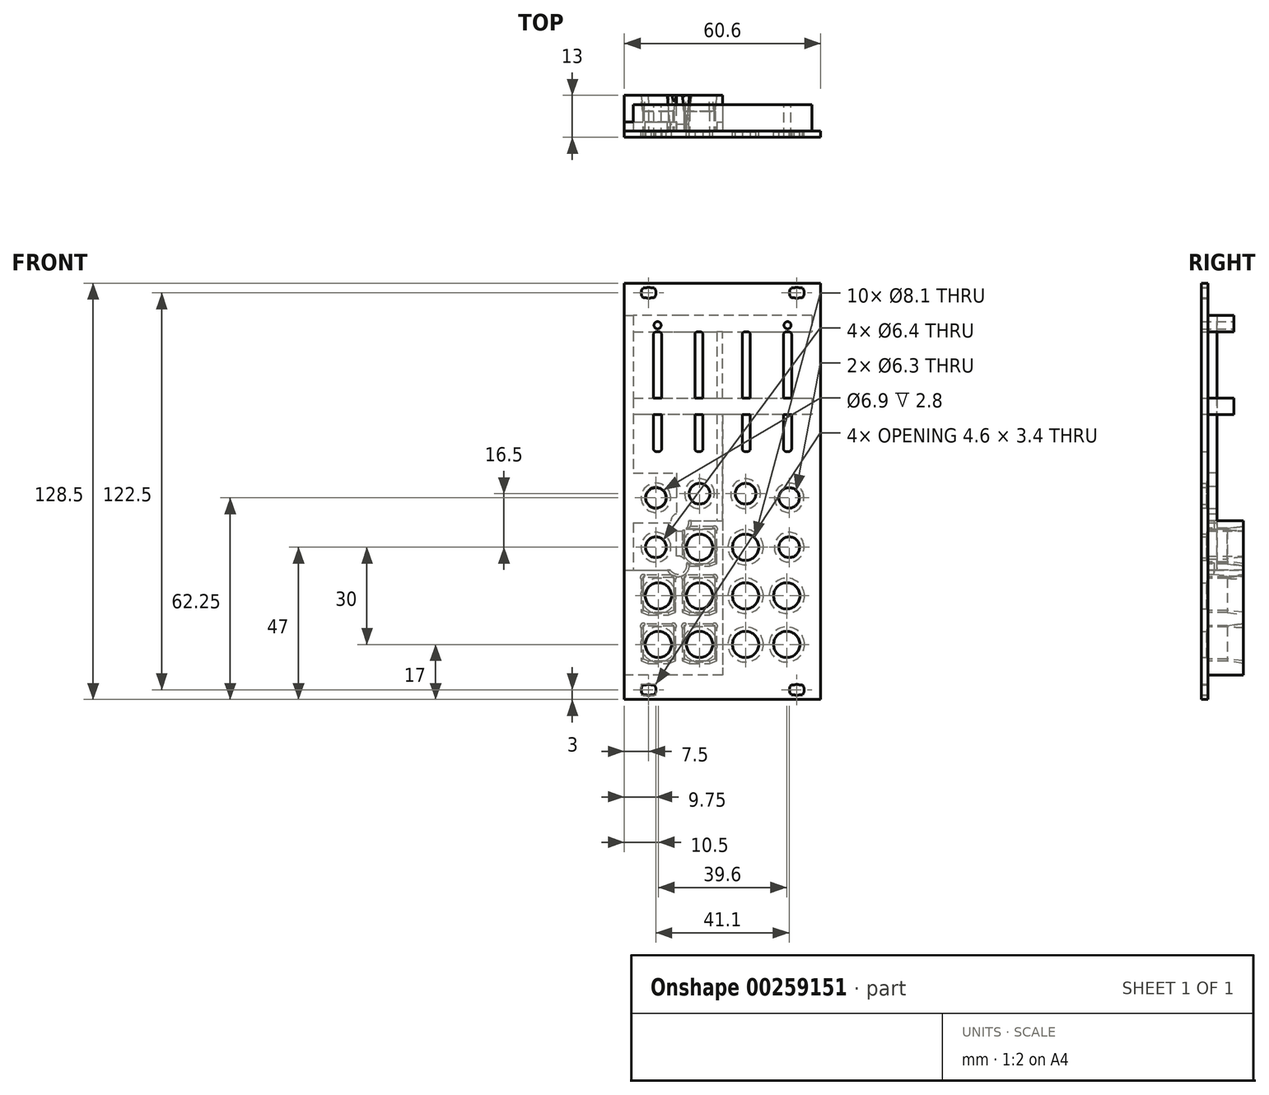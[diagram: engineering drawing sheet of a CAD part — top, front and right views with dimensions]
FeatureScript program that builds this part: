
annotation { "Feature Type Name" : "Feature", "Feature Type Description" : "" }
export const myFeature = defineFeature(function(context is Context, id is Id, definition is map)
    precondition{}
    {
        {
            var Q0;
            Q0=qCreatedBy(makeId("Front.planeOp"),FACE);
            var sketch = newSketch(context, id + "F0", { "sketchPlane" : qUnion([Q0])});
            skLineSegment(sketch, "E0", {"start": v(23.72, -59.75) * mm, "end": v(24.62, -59.75) * mm});
            skLineSegment(sketch, "E1", {"start": v(21.22, -59.75) * mm, "end": v(22.12, -59.75) * mm});
            skLineSegment(sketch, "E2", {"start": v(23.72, -62.75) * mm, "end": v(24.62, -62.75) * mm});
            skLineSegment(sketch, "E3", {"start": v(21.22, -62.75) * mm, "end": v(22.12, -62.75) * mm});
            skLineSegment(sketch, "E4", {"start": v(21.22, 59.75) * mm, "end": v(22.12, 59.75) * mm});
            skLineSegment(sketch, "E5", {"start": v(23.72, 59.75) * mm, "end": v(24.62, 59.75) * mm});
            skLineSegment(sketch, "E6", {"start": v(21.22, 62.75) * mm, "end": v(22.12, 62.75) * mm});
            skLineSegment(sketch, "E7", {"start": v(23.72, 62.75) * mm, "end": v(24.62, 62.75) * mm});
            skLineSegment(sketch, "E8", {"start": v(-30.3, -64.25) * mm, "end": v(-30.3, -61.25) * mm});
            skLineSegment(sketch, "E9", {"start": v(-30.3, 64.25) * mm, "end": v(30.3, 64.25) * mm});
            skLineSegment(sketch, "E10", {"start": v(30.3, -64.25) * mm, "end": v(30.3, 64.25) * mm});
            skLineSegment(sketch, "E11", {"start": v(-30.3, -64.25) * mm, "end": v(30.3, -64.25) * mm});
            skLineSegment(sketch, "E12", {"start": v(-30.3, -64.25) * mm, "end": v(-30.3, 64.25) * mm});
            skLineSegment(sketch, "E13", {"start": v(-22, -59.75) * mm, "end": v(-21.1, -59.75) * mm});
            skLineSegment(sketch, "E14", {"start": v(-24.5, -59.75) * mm, "end": v(-23.6, -59.75) * mm});
            skLineSegment(sketch, "E15", {"start": v(-22, -62.75) * mm, "end": v(-21.1, -62.75) * mm});
            skLineSegment(sketch, "E16", {"start": v(-24.5, -62.75) * mm, "end": v(-23.6, -62.75) * mm});
            skLineSegment(sketch, "E17", {"start": v(-22, 62.75) * mm, "end": v(-21.1, 62.75) * mm});
            skLineSegment(sketch, "E18", {"start": v(-24.5, 62.75) * mm, "end": v(-23.6, 62.75) * mm});
            skLineSegment(sketch, "E19", {"start": v(-22, 59.75) * mm, "end": v(-21.1, 59.75) * mm});
            skLineSegment(sketch, "E20", {"start": v(-24.5, 59.75) * mm, "end": v(-23.6, 59.75) * mm});
            skArc(sketch, "E21", {"start": v(21.22, -59.75) * mm, "mid": v(20.62, -61.25) * mm, "end": v(21.22, -62.75) * mm});
            skArc(sketch, "E22", {"start": v(24.62, -62.75) * mm, "mid": v(25.22, -61.25) * mm, "end": v(24.62, -59.75) * mm});
            skArc(sketch, "E23", {"start": v(23.72, -59.75) * mm, "mid": v(22.92, -59.55) * mm, "end": v(22.12, -59.75) * mm});
            skArc(sketch, "E24", {"start": v(22.12, -62.75) * mm, "mid": v(22.92, -62.95) * mm, "end": v(23.72, -62.75) * mm});
            skArc(sketch, "E25", {"start": v(22.12, 59.75) * mm, "mid": v(22.92, 59.55) * mm, "end": v(23.72, 59.75) * mm});
            skArc(sketch, "E26", {"start": v(23.72, 62.75) * mm, "mid": v(22.92, 62.95) * mm, "end": v(22.12, 62.75) * mm});
            skArc(sketch, "E27", {"start": v(24.62, 59.75) * mm, "mid": v(25.22, 61.25) * mm, "end": v(24.62, 62.75) * mm});
            skArc(sketch, "E28", {"start": v(21.22, 62.75) * mm, "mid": v(20.62, 61.25) * mm, "end": v(21.22, 59.75) * mm});
            skArc(sketch, "E29", {"start": v(-24.5, -59.75) * mm, "mid": v(-25.1, -61.25) * mm, "end": v(-24.5, -62.75) * mm});
            skArc(sketch, "E30", {"start": v(-21.1, -62.75) * mm, "mid": v(-20.5, -61.25) * mm, "end": v(-21.1, -59.75) * mm});
            skArc(sketch, "E31", {"start": v(-22, -59.75) * mm, "mid": v(-22.8, -59.55) * mm, "end": v(-23.6, -59.75) * mm});
            skArc(sketch, "E32", {"start": v(-23.6, -62.75) * mm, "mid": v(-22.8, -62.95) * mm, "end": v(-22, -62.75) * mm});
            skArc(sketch, "E33", {"start": v(-24.5, 62.75) * mm, "mid": v(-25.1, 61.25) * mm, "end": v(-24.5, 59.75) * mm});
            skArc(sketch, "E34", {"start": v(-21.1, 59.75) * mm, "mid": v(-20.5, 61.25) * mm, "end": v(-21.1, 62.75) * mm});
            skArc(sketch, "E35", {"start": v(-22, 62.75) * mm, "mid": v(-22.8, 62.95) * mm, "end": v(-23.6, 62.75) * mm});
            skArc(sketch, "E36", {"start": v(-23.6, 59.75) * mm, "mid": v(-22.8, 59.55) * mm, "end": v(-22, 59.75) * mm});
            skLineSegment(sketch, "E37", {"start": v(13.3, -22.75) * mm, "end": v(14.3, -22.75) * mm});
            skLineSegment(sketch, "E38", {"start": v(13.8, -23.25) * mm, "end": v(13.8, -22.25) * mm});
            skLineSegment(sketch, "E39", {"start": v(-20.55, -2.5) * mm, "end": v(-20.55, -1.5) * mm});
            skLineSegment(sketch, "E40", {"start": v(-21.05, -2) * mm, "end": v(-20.05, -2) * mm});
            skCircle(sketch, "E41", {"center": v(-20.55, -2) * mm, "radius": 3.15 * mm});
            skLineSegment(sketch, "E42", {"start": v(20.55, -2.5) * mm, "end": v(20.55, -1.5) * mm});
            skLineSegment(sketch, "E43", {"start": v(20.05, -2) * mm, "end": v(21.05, -2) * mm});
            skCircle(sketch, "E44", {"center": v(20.55, -2) * mm, "radius": 3.15 * mm});
            skLineSegment(sketch, "E45", {"start": v(6.05, 30.75) * mm, "end": v(6.05, 48.35) * mm});
            skLineSegment(sketch, "E46", {"start": v(6.05, 13.15) * mm, "end": v(6.05, 30.75) * mm});
            skLineSegment(sketch, "E47", {"start": v(6.95, 12.25) * mm, "end": v(7.65, 12.25) * mm});
            skLineSegment(sketch, "E48", {"start": v(7.3, 30.25) * mm, "end": v(7.3, 31.25) * mm});
            skLineSegment(sketch, "E49", {"start": v(8.55, 13.15) * mm, "end": v(8.55, 30.75) * mm});
            skLineSegment(sketch, "E50", {"start": v(6.8, 30.75) * mm, "end": v(7.8, 30.75) * mm});
            skLineSegment(sketch, "E51", {"start": v(6.95, 49.25) * mm, "end": v(7.65, 49.25) * mm});
            skLineSegment(sketch, "E52", {"start": v(8.55, 30.75) * mm, "end": v(8.55, 48.35) * mm});
            skArc(sketch, "E53", {"start": v(6.05, 13.15) * mm, "mid": v(6.31, 12.51) * mm, "end": v(6.95, 12.25) * mm});
            skArc(sketch, "E54", {"start": v(6.95, 49.25) * mm, "mid": v(6.31, 48.99) * mm, "end": v(6.05, 48.35) * mm});
            skArc(sketch, "E55", {"start": v(7.65, 12.25) * mm, "mid": v(8.29, 12.51) * mm, "end": v(8.55, 13.15) * mm});
            skArc(sketch, "E56", {"start": v(8.55, 48.35) * mm, "mid": v(8.29, 48.99) * mm, "end": v(7.65, 49.25) * mm});
            skLineSegment(sketch, "E57", {"start": v(-8.55, 30.75) * mm, "end": v(-8.55, 48.35) * mm});
            skLineSegment(sketch, "E58", {"start": v(-8.55, 13.15) * mm, "end": v(-8.55, 30.75) * mm});
            skLineSegment(sketch, "E59", {"start": v(-7.65, 12.25) * mm, "end": v(-6.95, 12.25) * mm});
            skLineSegment(sketch, "E60", {"start": v(-7.3, 30.25) * mm, "end": v(-7.3, 31.25) * mm});
            skLineSegment(sketch, "E61", {"start": v(-6.05, 13.15) * mm, "end": v(-6.05, 30.75) * mm});
            skLineSegment(sketch, "E62", {"start": v(-7.8, 30.75) * mm, "end": v(-6.8, 30.75) * mm});
            skLineSegment(sketch, "E63", {"start": v(-7.65, 49.25) * mm, "end": v(-6.95, 49.25) * mm});
            skLineSegment(sketch, "E64", {"start": v(-6.05, 30.75) * mm, "end": v(-6.05, 48.35) * mm});
            skArc(sketch, "E65", {"start": v(-8.55, 13.15) * mm, "mid": v(-8.29, 12.51) * mm, "end": v(-7.65, 12.25) * mm});
            skArc(sketch, "E66", {"start": v(-7.65, 49.25) * mm, "mid": v(-8.29, 48.99) * mm, "end": v(-8.55, 48.35) * mm});
            skArc(sketch, "E67", {"start": v(-6.95, 12.25) * mm, "mid": v(-6.31, 12.51) * mm, "end": v(-6.05, 13.15) * mm});
            skArc(sketch, "E68", {"start": v(-6.05, 48.35) * mm, "mid": v(-6.31, 48.99) * mm, "end": v(-6.95, 49.25) * mm});
            skLineSegment(sketch, "E69", {"start": v(18.8, 30.75) * mm, "end": v(18.8, 48.35) * mm});
            skLineSegment(sketch, "E70", {"start": v(18.8, 13.15) * mm, "end": v(18.8, 30.75) * mm});
            skLineSegment(sketch, "E71", {"start": v(19.7, 12.25) * mm, "end": v(20.4, 12.25) * mm});
            skLineSegment(sketch, "E72", {"start": v(20.05, 30.25) * mm, "end": v(20.05, 31.25) * mm});
            skLineSegment(sketch, "E73", {"start": v(21.3, 13.15) * mm, "end": v(21.3, 30.75) * mm});
            skLineSegment(sketch, "E74", {"start": v(19.55, 30.75) * mm, "end": v(20.55, 30.75) * mm});
            skLineSegment(sketch, "E75", {"start": v(19.7, 49.25) * mm, "end": v(20.4, 49.25) * mm});
            skLineSegment(sketch, "E76", {"start": v(21.3, 30.75) * mm, "end": v(21.3, 48.35) * mm});
            skArc(sketch, "E77", {"start": v(18.8, 13.15) * mm, "mid": v(19.06, 12.51) * mm, "end": v(19.7, 12.25) * mm});
            skArc(sketch, "E78", {"start": v(19.7, 49.25) * mm, "mid": v(19.06, 48.99) * mm, "end": v(18.8, 48.35) * mm});
            skArc(sketch, "E79", {"start": v(20.4, 12.25) * mm, "mid": v(21.04, 12.51) * mm, "end": v(21.3, 13.15) * mm});
            skArc(sketch, "E80", {"start": v(21.3, 48.35) * mm, "mid": v(21.04, 48.99) * mm, "end": v(20.4, 49.25) * mm});
            skLineSegment(sketch, "E81", {"start": v(-21.3, 30.75) * mm, "end": v(-21.3, 48.35) * mm});
            skLineSegment(sketch, "E82", {"start": v(-21.3, 13.15) * mm, "end": v(-21.3, 30.75) * mm});
            skLineSegment(sketch, "E83", {"start": v(-20.4, 12.25) * mm, "end": v(-19.7, 12.25) * mm});
            skLineSegment(sketch, "E84", {"start": v(-20.05, 30.25) * mm, "end": v(-20.05, 31.25) * mm});
            skLineSegment(sketch, "E85", {"start": v(-18.8, 13.15) * mm, "end": v(-18.8, 30.75) * mm});
            skLineSegment(sketch, "E86", {"start": v(-20.55, 30.75) * mm, "end": v(-19.55, 30.75) * mm});
            skLineSegment(sketch, "E87", {"start": v(-20.4, 49.25) * mm, "end": v(-19.7, 49.25) * mm});
            skLineSegment(sketch, "E88", {"start": v(-18.8, 30.75) * mm, "end": v(-18.8, 48.35) * mm});
            skArc(sketch, "E89", {"start": v(-21.3, 13.15) * mm, "mid": v(-21.04, 12.51) * mm, "end": v(-20.4, 12.25) * mm});
            skArc(sketch, "E90", {"start": v(-20.4, 49.25) * mm, "mid": v(-21.04, 48.99) * mm, "end": v(-21.3, 48.35) * mm});
            skArc(sketch, "E91", {"start": v(-19.7, 12.25) * mm, "mid": v(-19.06, 12.51) * mm, "end": v(-18.8, 13.15) * mm});
            skArc(sketch, "E92", {"start": v(-18.8, 48.35) * mm, "mid": v(-19.06, 48.99) * mm, "end": v(-19.7, 49.25) * mm});
            skCircle(sketch, "E93", {"center": v(-20.05, 51.25) * mm, "radius": 1.1 * mm});
            skLineSegment(sketch, "E94", {"start": v(-14.3, -22.75) * mm, "end": v(-13.3, -22.75) * mm});
            skLineSegment(sketch, "E95", {"start": v(-13.8, -23.25) * mm, "end": v(-13.8, -22.25) * mm});
            skLineSegment(sketch, "E96", {"start": v(13.2, -10) * mm, "end": v(13.2, -9) * mm});
            skLineSegment(sketch, "E97", {"start": v(12.7, -9.5) * mm, "end": v(13.7, -9.5) * mm});
            skLineSegment(sketch, "E98", {"start": v(-13.2, -10) * mm, "end": v(-13.2, -9) * mm});
            skLineSegment(sketch, "E99", {"start": v(-13.7, -9.5) * mm, "end": v(-12.7, -9.5) * mm});
            skLineSegment(sketch, "E100", {"start": v(7.1, -1.25) * mm, "end": v(7.1, -0.25) * mm});
            skLineSegment(sketch, "E101", {"start": v(6.6, -0.75) * mm, "end": v(7.6, -0.75) * mm});
            skCircle(sketch, "E102", {"center": v(7.1, -0.75) * mm, "radius": 3.2 * mm});
            skLineSegment(sketch, "E103", {"start": v(-7.1, -1.25) * mm, "end": v(-7.1, -0.25) * mm});
            skLineSegment(sketch, "E104", {"start": v(-7.6, -0.75) * mm, "end": v(-6.6, -0.75) * mm});
            skCircle(sketch, "E105", {"center": v(-7.1, -0.75) * mm, "radius": 3.2 * mm});
            skLineSegment(sketch, "E106", {"start": v(20.55, -17.75) * mm, "end": v(20.55, -16.75) * mm});
            skLineSegment(sketch, "E107", {"start": v(20.05, -17.25) * mm, "end": v(21.05, -17.25) * mm});
            skCircle(sketch, "E108", {"center": v(20.55, -17.25) * mm, "radius": 3.2 * mm});
            skLineSegment(sketch, "E109", {"start": v(-20.55, -17.75) * mm, "end": v(-20.55, -16.75) * mm});
            skLineSegment(sketch, "E110", {"start": v(-21.05, -17.25) * mm, "end": v(-20.05, -17.25) * mm});
            skCircle(sketch, "E111", {"center": v(-20.55, -17.25) * mm, "radius": 3.2 * mm});
            skLineSegment(sketch, "E112", {"start": v(6.35, -17.25) * mm, "end": v(7.85, -17.25) * mm});
            skLineSegment(sketch, "E113", {"start": v(7.1, -18) * mm, "end": v(7.1, -16.5) * mm});
            skCircle(sketch, "E114", {"center": v(7.1, -17.25) * mm, "radius": 4.05 * mm});
            skLineSegment(sketch, "E115", {"start": v(19.05, -32.25) * mm, "end": v(20.55, -32.25) * mm});
            skLineSegment(sketch, "E116", {"start": v(19.8, -33) * mm, "end": v(19.8, -31.5) * mm});
            skCircle(sketch, "E117", {"center": v(19.8, -32.25) * mm, "radius": 4.05 * mm});
            skLineSegment(sketch, "E118", {"start": v(6.35, -32.25) * mm, "end": v(7.85, -32.25) * mm});
            skLineSegment(sketch, "E119", {"start": v(7.1, -33) * mm, "end": v(7.1, -31.5) * mm});
            skCircle(sketch, "E120", {"center": v(7.1, -32.25) * mm, "radius": 4.05 * mm});
            skLineSegment(sketch, "E121", {"start": v(19.05, -47.25) * mm, "end": v(20.55, -47.25) * mm});
            skLineSegment(sketch, "E122", {"start": v(19.8, -48) * mm, "end": v(19.8, -46.5) * mm});
            skCircle(sketch, "E123", {"center": v(19.8, -47.25) * mm, "radius": 4.05 * mm});
            skLineSegment(sketch, "E124", {"start": v(6.35, -47.25) * mm, "end": v(7.85, -47.25) * mm});
            skLineSegment(sketch, "E125", {"start": v(7.1, -48) * mm, "end": v(7.1, -46.5) * mm});
            skCircle(sketch, "E126", {"center": v(7.1, -47.25) * mm, "radius": 4.05 * mm});
            skLineSegment(sketch, "E127", {"start": v(-7.85, -17.25) * mm, "end": v(-6.35, -17.25) * mm});
            skLineSegment(sketch, "E128", {"start": v(-7.1, -18) * mm, "end": v(-7.1, -16.5) * mm});
            skCircle(sketch, "E129", {"center": v(-7.1, -17.25) * mm, "radius": 4.05 * mm});
            skLineSegment(sketch, "E130", {"start": v(-20.55, -32.25) * mm, "end": v(-19.05, -32.25) * mm});
            skLineSegment(sketch, "E131", {"start": v(-19.8, -33) * mm, "end": v(-19.8, -31.5) * mm});
            skCircle(sketch, "E132", {"center": v(-19.8, -32.25) * mm, "radius": 4.05 * mm});
            skLineSegment(sketch, "E133", {"start": v(-7.85, -32.25) * mm, "end": v(-6.35, -32.25) * mm});
            skLineSegment(sketch, "E134", {"start": v(-7.1, -33) * mm, "end": v(-7.1, -31.5) * mm});
            skCircle(sketch, "E135", {"center": v(-7.1, -32.25) * mm, "radius": 4.05 * mm});
            skLineSegment(sketch, "E136", {"start": v(-20.55, -47.25) * mm, "end": v(-19.05, -47.25) * mm});
            skLineSegment(sketch, "E137", {"start": v(-19.8, -48) * mm, "end": v(-19.8, -46.5) * mm});
            skCircle(sketch, "E138", {"center": v(-19.8, -47.25) * mm, "radius": 4.05 * mm});
            skLineSegment(sketch, "E139", {"start": v(-7.85, -47.25) * mm, "end": v(-6.35, -47.25) * mm});
            skLineSegment(sketch, "E140", {"start": v(-7.1, -48) * mm, "end": v(-7.1, -46.5) * mm});
            skCircle(sketch, "E141", {"center": v(-7.1, -47.25) * mm, "radius": 4.05 * mm});
            skLineSegment(sketch, "E142", {"start": v(19.42, 51.25) * mm, "end": v(20.69, 51.25) * mm});
            skLineSegment(sketch, "E143", {"start": v(20.05, 50.62) * mm, "end": v(20.05, 51.89) * mm});
            skCircle(sketch, "E144", {"center": v(20.05, 51.25) * mm, "radius": 1.1 * mm});
            skLineSegment(sketch, "E145", {"start": v(-20.69, 51.25) * mm, "end": v(-19.41, 51.25) * mm});
            skLineSegment(sketch, "E146", {"start": v(-20.05, 50.62) * mm, "end": v(-20.05, 51.89) * mm});
            skCircle(sketch, "E147", {"center": v(-13.8, -22.75) * mm, "radius": 0.75 * mm, "construction": true});
            skCircle(sketch, "E148", {"center": v(-13.2, -9.5) * mm, "radius": 1 * mm, "construction": true});
            skCircle(sketch, "E149", {"center": v(13.2, -9.5) * mm, "radius": 1 * mm, "construction": true});
            skCircle(sketch, "E150", {"center": v(13.8, -22.75) * mm, "radius": 0.75 * mm, "construction": true});
            skSolve(sketch);
        }
        {
            var Q0;
            Q0=qSketchRegion(id+"F0",true);
            extrude(context, id + "F1", {"entities" : qUnion([Q0]), "depth" : 2 * mm});
        }
        {
            var Q0;
            Q0=makeQuery(id+"F1.opExtrude","CAP_FACE",FACE,{"disambiguationData":[OSD([sQuery(id+"F0.wireOp",EDGE,"E0"),sQuery(id+"F0.wireOp",EDGE,"E1"),sQuery(id+"F0.wireOp",EDGE,"E2"),sQuery(id+"F0.wireOp",EDGE,"E3"),sQuery(id+"F0.wireOp",EDGE,"E4"),sQuery(id+"F0.wireOp",EDGE,"E5"),sQuery(id+"F0.wireOp",EDGE,"E6"),sQuery(id+"F0.wireOp",EDGE,"E7"),sQuery(id+"F0.wireOp",EDGE,"E9"),sQuery(id+"F0.wireOp",EDGE,"E10"),sQuery(id+"F0.wireOp",EDGE,"E11"),sQuery(id+"F0.wireOp",EDGE,"E12"),sQuery(id+"F0.wireOp",EDGE,"E13"),sQuery(id+"F0.wireOp",EDGE,"E14"),sQuery(id+"F0.wireOp",EDGE,"E15"),sQuery(id+"F0.wireOp",EDGE,"E16"),sQuery(id+"F0.wireOp",EDGE,"E17"),sQuery(id+"F0.wireOp",EDGE,"E18"),sQuery(id+"F0.wireOp",EDGE,"E19"),sQuery(id+"F0.wireOp",EDGE,"E20"),sQuery(id+"F0.wireOp",EDGE,"E21"),sQuery(id+"F0.wireOp",EDGE,"E22"),sQuery(id+"F0.wireOp",EDGE,"E23"),sQuery(id+"F0.wireOp",EDGE,"E24"),sQuery(id+"F0.wireOp",EDGE,"E25"),sQuery(id+"F0.wireOp",EDGE,"E26"),sQuery(id+"F0.wireOp",EDGE,"E27"),sQuery(id+"F0.wireOp",EDGE,"E28"),sQuery(id+"F0.wireOp",EDGE,"E29"),sQuery(id+"F0.wireOp",EDGE,"E30"),sQuery(id+"F0.wireOp",EDGE,"E31"),sQuery(id+"F0.wireOp",EDGE,"E32"),sQuery(id+"F0.wireOp",EDGE,"E33"),sQuery(id+"F0.wireOp",EDGE,"E34"),sQuery(id+"F0.wireOp",EDGE,"E35"),sQuery(id+"F0.wireOp",EDGE,"E36"),sQuery(id+"F0.wireOp",EDGE,"E41"),sQuery(id+"F0.wireOp",EDGE,"E44"),sQuery(id+"F0.wireOp",EDGE,"E45"),sQuery(id+"F0.wireOp",EDGE,"E46"),sQuery(id+"F0.wireOp",EDGE,"E47"),sQuery(id+"F0.wireOp",EDGE,"E49"),sQuery(id+"F0.wireOp",EDGE,"E51"),sQuery(id+"F0.wireOp",EDGE,"E52"),sQuery(id+"F0.wireOp",EDGE,"E53"),sQuery(id+"F0.wireOp",EDGE,"E54"),sQuery(id+"F0.wireOp",EDGE,"E55"),sQuery(id+"F0.wireOp",EDGE,"E56"),sQuery(id+"F0.wireOp",EDGE,"E57"),sQuery(id+"F0.wireOp",EDGE,"E58"),sQuery(id+"F0.wireOp",EDGE,"E59"),sQuery(id+"F0.wireOp",EDGE,"E61"),sQuery(id+"F0.wireOp",EDGE,"E63"),sQuery(id+"F0.wireOp",EDGE,"E64"),sQuery(id+"F0.wireOp",EDGE,"E65"),sQuery(id+"F0.wireOp",EDGE,"E66"),sQuery(id+"F0.wireOp",EDGE,"E67"),sQuery(id+"F0.wireOp",EDGE,"E68"),sQuery(id+"F0.wireOp",EDGE,"E69"),sQuery(id+"F0.wireOp",EDGE,"E70"),sQuery(id+"F0.wireOp",EDGE,"E71"),sQuery(id+"F0.wireOp",EDGE,"E73"),sQuery(id+"F0.wireOp",EDGE,"E75"),sQuery(id+"F0.wireOp",EDGE,"E76"),sQuery(id+"F0.wireOp",EDGE,"E77"),sQuery(id+"F0.wireOp",EDGE,"E78"),sQuery(id+"F0.wireOp",EDGE,"E79"),sQuery(id+"F0.wireOp",EDGE,"E80"),sQuery(id+"F0.wireOp",EDGE,"E81"),sQuery(id+"F0.wireOp",EDGE,"E82"),sQuery(id+"F0.wireOp",EDGE,"E83"),sQuery(id+"F0.wireOp",EDGE,"E85"),sQuery(id+"F0.wireOp",EDGE,"E87"),sQuery(id+"F0.wireOp",EDGE,"E88"),sQuery(id+"F0.wireOp",EDGE,"E89"),sQuery(id+"F0.wireOp",EDGE,"E90"),sQuery(id+"F0.wireOp",EDGE,"E91"),sQuery(id+"F0.wireOp",EDGE,"E92"),sQuery(id+"F0.wireOp",EDGE,"E93"),sQuery(id+"F0.wireOp",EDGE,"E102"),sQuery(id+"F0.wireOp",EDGE,"E105"),sQuery(id+"F0.wireOp",EDGE,"E108"),sQuery(id+"F0.wireOp",EDGE,"E111"),sQuery(id+"F0.wireOp",EDGE,"E114"),sQuery(id+"F0.wireOp",EDGE,"E117"),sQuery(id+"F0.wireOp",EDGE,"E120"),sQuery(id+"F0.wireOp",EDGE,"E123"),sQuery(id+"F0.wireOp",EDGE,"E126"),sQuery(id+"F0.wireOp",EDGE,"E129"),sQuery(id+"F0.wireOp",EDGE,"E132"),sQuery(id+"F0.wireOp",EDGE,"E135"),sQuery(id+"F0.wireOp",EDGE,"E138"),sQuery(id+"F0.wireOp",EDGE,"E141"),sQuery(id+"F0.wireOp",EDGE,"E144"),sQuery(id+"F0.wireOp",EDGE,"E147"),sQuery(id+"F0.wireOp",EDGE,"E148"),sQuery(id+"F0.wireOp",EDGE,"E149"),sQuery(id+"F0.wireOp",EDGE,"E150")])],"isStart":true});
            var sketch = newSketch(context, id + "F2", { "sketchPlane" : qUnion([Q0])});
            skLineSegment(sketch, "E151.bottom", {"start": v(-27.51, 54.25) * mm, "end": v(-12.59, 54.25) * mm});
            skLineSegment(sketch, "E151.top", {"start": v(-27.51, 49.25) * mm, "end": v(-12.59, 49.25) * mm});
            skLineSegment(sketch, "E151.left", {"start": v(-27.51, 54.25) * mm, "end": v(-27.51, 49.25) * mm});
            skLineSegment(sketch, "E152", {"start": v(0, 64.25) * mm, "end": v(0, -64.25) * mm, "construction": true});
            skLineSegment(sketch, "E153", {"start": v(-20.05, 54.25) * mm, "end": v(-20.05, 49.25) * mm, "construction": true});
            skPoint(sketch, "E154", {"position": v(-20.05, 51.25) * mm});
            skLineSegment(sketch, "E155.MirrorCS", {"start": v(-12.59, 54.25) * mm, "end": v(-27.51, 54.25) * mm});
            skLineSegment(sketch, "E156.MirrorCS", {"start": v(-12.59, 49.25) * mm, "end": v(-27.51, 49.25) * mm});
            skLineSegment(sketch, "E157.MirrorCS", {"start": v(-40.1, 64.25) * mm, "end": v(-40.1, -64.25) * mm, "construction": true});
            skLineSegment(sketch, "E158.MirrorCS", {"start": v(12.59, 54.25) * mm, "end": v(27.51, 54.25) * mm});
            skLineSegment(sketch, "E159.MirrorCS", {"start": v(27.51, 54.25) * mm, "end": v(27.51, 49.25) * mm});
            skLineSegment(sketch, "E160.MirrorCS", {"start": v(27.51, 49.25) * mm, "end": v(12.59, 49.25) * mm});
            skPoint(sketch, "E161.MirrorP", {"position": v(20.05, 51.25) * mm});
            skCircle(sketch, "E162.0", {"center": v(-20.05, 51.25) * mm, "radius": 1.1 * mm});
            skCircle(sketch, "E163.0", {"center": v(20.05, 51.25) * mm, "radius": 1.1 * mm});
            skLineSegment(sketch, "E164", {"start": v(-27.51, 28.73) * mm, "end": v(-27.51, 23.73) * mm});
            skLineSegment(sketch, "E165", {"start": v(-27.51, 23.73) * mm, "end": v(27.51, 23.73) * mm});
            skLineSegment(sketch, "E166", {"start": v(27.51, 23.73) * mm, "end": v(27.51, 28.73) * mm});
            skLineSegment(sketch, "E167", {"start": v(15.84, 28.73) * mm, "end": v(-12.59, 28.73) * mm});
            skLineSegment(sketch, "E168", {"start": v(-12.59, 28.73) * mm, "end": v(-27.51, 28.73) * mm});
            skLineSegment(sketch, "E169", {"start": v(15.84, 28.73) * mm, "end": v(27.51, 28.73) * mm});
            skLineSegment(sketch, "E170", {"start": v(-12.59, 54.25) * mm, "end": v(12.59, 54.25) * mm});
            skLineSegment(sketch, "E171", {"start": v(12.59, 49.25) * mm, "end": v(-12.59, 49.25) * mm});
            skSolve(sketch);
        }
        {
            var Q0;
            Q0=qSketchRegion(id+"F2",true);
            extrude(context, id + "F3", {"entities" : qUnion([Q0]), "operationType" : NewBodyOperationType.ADD, "depth" : 8.1 * mm, "offsetDistance" : 25 * mm});
        }
        {
            var Q0;
            Q0=makeQuery(id+"F1.opExtrude","CAP_EDGE",EDGE,{"disambiguationData":[OSD([sQuery(id+"F0.wireOp",EDGE,"E44")])],"isStart":true});
            var Q1;
            Q1=makeQuery(id+"F1.opExtrude","CAP_EDGE",EDGE,{"disambiguationData":[OSD([sQuery(id+"F0.wireOp",EDGE,"E102")])],"isStart":true});
            var Q2;
            Q2=makeQuery(id+"F1.opExtrude","CAP_EDGE",EDGE,{"disambiguationData":[OSD([sQuery(id+"F0.wireOp",EDGE,"E105")])],"isStart":true});
            var Q3;
            Q3=makeQuery(id+"F1.opExtrude","CAP_EDGE",EDGE,{"disambiguationData":[OSD([sQuery(id+"F0.wireOp",EDGE,"E41")])],"isStart":true});
            var Q4;
            Q4=makeQuery(id+"F1.opExtrude","CAP_EDGE",EDGE,{"disambiguationData":[OSD([sQuery(id+"F0.wireOp",EDGE,"E111")])],"isStart":true});
            var Q5;
            Q5=makeQuery(id+"F1.opExtrude","CAP_EDGE",EDGE,{"disambiguationData":[OSD([sQuery(id+"F0.wireOp",EDGE,"E129")])],"isStart":true});
            var Q6;
            Q6=makeQuery(id+"F1.opExtrude","CAP_EDGE",EDGE,{"disambiguationData":[OSD([sQuery(id+"F0.wireOp",EDGE,"E135")])],"isStart":true});
            var Q7;
            Q7=makeQuery(id+"F1.opExtrude","CAP_EDGE",EDGE,{"disambiguationData":[OSD([sQuery(id+"F0.wireOp",EDGE,"E114")])],"isStart":true});
            var Q8;
            Q8=makeQuery(id+"F1.opExtrude","CAP_EDGE",EDGE,{"disambiguationData":[OSD([sQuery(id+"F0.wireOp",EDGE,"E108")])],"isStart":true});
            var Q9;
            Q9=makeQuery(id+"F1.opExtrude","CAP_EDGE",EDGE,{"disambiguationData":[OSD([sQuery(id+"F0.wireOp",EDGE,"E117")])],"isStart":true});
            var Q10;
            Q10=makeQuery(id+"F1.opExtrude","CAP_EDGE",EDGE,{"disambiguationData":[OSD([sQuery(id+"F0.wireOp",EDGE,"E120")])],"isStart":true});
            var Q11;
            Q11=makeQuery(id+"F1.opExtrude","CAP_EDGE",EDGE,{"disambiguationData":[OSD([sQuery(id+"F0.wireOp",EDGE,"E132")])],"isStart":true});
            var Q12;
            Q12=makeQuery(id+"F1.opExtrude","CAP_EDGE",EDGE,{"disambiguationData":[OSD([sQuery(id+"F0.wireOp",EDGE,"E141")])],"isStart":true});
            var Q13;
            Q13=makeQuery(id+"F1.opExtrude","CAP_EDGE",EDGE,{"disambiguationData":[OSD([sQuery(id+"F0.wireOp",EDGE,"E126")])],"isStart":true});
            var Q14;
            Q14=makeQuery(id+"F1.opExtrude","CAP_EDGE",EDGE,{"disambiguationData":[OSD([sQuery(id+"F0.wireOp",EDGE,"E123")])],"isStart":true});
            var Q15;
            Q15=makeQuery(id+"F1.opExtrude","CAP_EDGE",EDGE,{"disambiguationData":[OSD([sQuery(id+"F0.wireOp",EDGE,"E138")])],"isStart":true});
            chamfer(context, id + "F4", {"entities" : qUnion([Q0, Q1, Q2, Q3, Q4, Q5, Q6, Q7, Q8, Q9, Q10, Q11, Q12, Q13, Q14, Q15]), "chamferType" : ChamferType.OFFSET_ANGLE, "width" : 1.4 * mm, "oppositeDirection" : false, "angle" : 12 * degree, "tangentPropagation" : true});
        }
        {
            var Q0;
            {var subQ0=sQuery(id+"F2.wireOp",EDGE,"E165");var subQ1=sQuery(id+"F0.wireOp",EDGE,"E82");var subQ2=sQuery(id+"F0.wireOp",EDGE,"E81");var subQ5=sQuery(id+"F2.wireOp",EDGE,"E169");var subQ6=sQuery(id+"F2.wireOp",EDGE,"E168");var subQ7=sQuery(id+"F2.wireOp",EDGE,"E167");Q0=makeQuery(id+"F3.boolean.opBoolean","SPLIT",FACE,{"disambiguationData":[TD([makeQuery(id+"F1.opExtrude","SWEPT_FACE",FACE,{"disambiguationData":[OSD([subQ2,subQ1])]})])],"derivedFrom":makeQuery(id+"F3.opExtrude","CAP_FACE",FACE,{"disambiguationData":[OSD([sQuery(id+"F2.wireOp",EDGE,"E164"),subQ0,sQuery(id+"F2.wireOp",EDGE,"E166"),subQ7,subQ6,subQ5])],"isStart":true})});}
            var sketch = newSketch(context, id + "F5", { "sketchPlane" : qUnion([Q0])});
            skLineSegment(sketch, "E172.0", {"start": v(-15.84, 28.73) * mm, "end": v(-27.51, 28.73) * mm});
            skLineSegment(sketch, "E173.0", {"start": v(-15.84, 28.73) * mm, "end": v(12.59, 28.73) * mm});
            skLineSegment(sketch, "E174.0", {"start": v(12.59, 28.73) * mm, "end": v(27.51, 28.73) * mm});
            skLineSegment(sketch, "E175.0", {"start": v(27.51, 28.73) * mm, "end": v(27.51, 23.73) * mm});
            skLineSegment(sketch, "E176.0", {"start": v(27.51, 23.73) * mm, "end": v(-27.51, 23.73) * mm});
            skLineSegment(sketch, "E177.0", {"start": v(-27.51, 23.73) * mm, "end": v(-27.51, 28.73) * mm});
            skSolve(sketch);
        }
        {
            var Q0;
            Q0 = qSketchRegion(id + "F5", true);
            var Q1;
            Q1=makeQuery(id+"F1.opExtrude","CAP_FACE",FACE,{"disambiguationData":[OSD([sQuery(id+"F0.wireOp",EDGE,"E0"),sQuery(id+"F0.wireOp",EDGE,"E1"),sQuery(id+"F0.wireOp",EDGE,"E2"),sQuery(id+"F0.wireOp",EDGE,"E3"),sQuery(id+"F0.wireOp",EDGE,"E4"),sQuery(id+"F0.wireOp",EDGE,"E5"),sQuery(id+"F0.wireOp",EDGE,"E6"),sQuery(id+"F0.wireOp",EDGE,"E7"),sQuery(id+"F0.wireOp",EDGE,"E9"),sQuery(id+"F0.wireOp",EDGE,"E10"),sQuery(id+"F0.wireOp",EDGE,"E11"),sQuery(id+"F0.wireOp",EDGE,"E12"),sQuery(id+"F0.wireOp",EDGE,"E13"),sQuery(id+"F0.wireOp",EDGE,"E14"),sQuery(id+"F0.wireOp",EDGE,"E15"),sQuery(id+"F0.wireOp",EDGE,"E16"),sQuery(id+"F0.wireOp",EDGE,"E17"),sQuery(id+"F0.wireOp",EDGE,"E18"),sQuery(id+"F0.wireOp",EDGE,"E19"),sQuery(id+"F0.wireOp",EDGE,"E20"),sQuery(id+"F0.wireOp",EDGE,"E21"),sQuery(id+"F0.wireOp",EDGE,"E22"),sQuery(id+"F0.wireOp",EDGE,"E23"),sQuery(id+"F0.wireOp",EDGE,"E24"),sQuery(id+"F0.wireOp",EDGE,"E25"),sQuery(id+"F0.wireOp",EDGE,"E26"),sQuery(id+"F0.wireOp",EDGE,"E27"),sQuery(id+"F0.wireOp",EDGE,"E28"),sQuery(id+"F0.wireOp",EDGE,"E29"),sQuery(id+"F0.wireOp",EDGE,"E30"),sQuery(id+"F0.wireOp",EDGE,"E31"),sQuery(id+"F0.wireOp",EDGE,"E32"),sQuery(id+"F0.wireOp",EDGE,"E33"),sQuery(id+"F0.wireOp",EDGE,"E34"),sQuery(id+"F0.wireOp",EDGE,"E35"),sQuery(id+"F0.wireOp",EDGE,"E36"),sQuery(id+"F0.wireOp",EDGE,"E41"),sQuery(id+"F0.wireOp",EDGE,"E44"),sQuery(id+"F0.wireOp",EDGE,"E45"),sQuery(id+"F0.wireOp",EDGE,"E46"),sQuery(id+"F0.wireOp",EDGE,"E47"),sQuery(id+"F0.wireOp",EDGE,"E49"),sQuery(id+"F0.wireOp",EDGE,"E51"),sQuery(id+"F0.wireOp",EDGE,"E52"),sQuery(id+"F0.wireOp",EDGE,"E53"),sQuery(id+"F0.wireOp",EDGE,"E54"),sQuery(id+"F0.wireOp",EDGE,"E55"),sQuery(id+"F0.wireOp",EDGE,"E56"),sQuery(id+"F0.wireOp",EDGE,"E57"),sQuery(id+"F0.wireOp",EDGE,"E58"),sQuery(id+"F0.wireOp",EDGE,"E59"),sQuery(id+"F0.wireOp",EDGE,"E61"),sQuery(id+"F0.wireOp",EDGE,"E63"),sQuery(id+"F0.wireOp",EDGE,"E64"),sQuery(id+"F0.wireOp",EDGE,"E65"),sQuery(id+"F0.wireOp",EDGE,"E66"),sQuery(id+"F0.wireOp",EDGE,"E67"),sQuery(id+"F0.wireOp",EDGE,"E68"),sQuery(id+"F0.wireOp",EDGE,"E69"),sQuery(id+"F0.wireOp",EDGE,"E70"),sQuery(id+"F0.wireOp",EDGE,"E71"),sQuery(id+"F0.wireOp",EDGE,"E73"),sQuery(id+"F0.wireOp",EDGE,"E75"),sQuery(id+"F0.wireOp",EDGE,"E76"),sQuery(id+"F0.wireOp",EDGE,"E77"),sQuery(id+"F0.wireOp",EDGE,"E78"),sQuery(id+"F0.wireOp",EDGE,"E79"),sQuery(id+"F0.wireOp",EDGE,"E80"),sQuery(id+"F0.wireOp",EDGE,"E81"),sQuery(id+"F0.wireOp",EDGE,"E82"),sQuery(id+"F0.wireOp",EDGE,"E83"),sQuery(id+"F0.wireOp",EDGE,"E85"),sQuery(id+"F0.wireOp",EDGE,"E87"),sQuery(id+"F0.wireOp",EDGE,"E88"),sQuery(id+"F0.wireOp",EDGE,"E89"),sQuery(id+"F0.wireOp",EDGE,"E90"),sQuery(id+"F0.wireOp",EDGE,"E91"),sQuery(id+"F0.wireOp",EDGE,"E92"),sQuery(id+"F0.wireOp",EDGE,"E93"),sQuery(id+"F0.wireOp",EDGE,"E102"),sQuery(id+"F0.wireOp",EDGE,"E105"),sQuery(id+"F0.wireOp",EDGE,"E108"),sQuery(id+"F0.wireOp",EDGE,"E111"),sQuery(id+"F0.wireOp",EDGE,"E114"),sQuery(id+"F0.wireOp",EDGE,"E117"),sQuery(id+"F0.wireOp",EDGE,"E120"),sQuery(id+"F0.wireOp",EDGE,"E123"),sQuery(id+"F0.wireOp",EDGE,"E126"),sQuery(id+"F0.wireOp",EDGE,"E129"),sQuery(id+"F0.wireOp",EDGE,"E132"),sQuery(id+"F0.wireOp",EDGE,"E135"),sQuery(id+"F0.wireOp",EDGE,"E138"),sQuery(id+"F0.wireOp",EDGE,"E141"),sQuery(id+"F0.wireOp",EDGE,"E144")])],"isStart":false});
            extrude(context, id + "F6", {"entities" : qUnion([Q0]), "operationType" : NewBodyOperationType.ADD, "endBound" : BoundingType.UP_TO_SURFACE, "depth" : 25 * mm, "endBoundEntityFace" : qUnion([Q1]), "offsetDistance" : 25 * mm});
        }
        {
            var Q0;
            {var subQ0=sQuery(id+"F0.wireOp",EDGE,"E59");var subQ1=sQuery(id+"F0.wireOp",EDGE,"E58");var subQ2=sQuery(id+"F0.wireOp",EDGE,"E57");var subQ3=sQuery(id+"F0.wireOp",EDGE,"E55");var subQ4=sQuery(id+"F0.wireOp",EDGE,"E53");var subQ5=sQuery(id+"F0.wireOp",EDGE,"E51");var subQ6=sQuery(id+"F0.wireOp",EDGE,"E52");var subQ7=sQuery(id+"F0.wireOp",EDGE,"E49");var subQ8=sQuery(id+"F0.wireOp",EDGE,"E47");var subQ9=sQuery(id+"F0.wireOp",EDGE,"E46");var subQ10=sQuery(id+"F0.wireOp",EDGE,"E45");var subQ11=sQuery(id+"F0.wireOp",EDGE,"E44");var subQ12=sQuery(id+"F0.wireOp",EDGE,"E41");var subQ13=sQuery(id+"F0.wireOp",EDGE,"E36");var subQ14=sQuery(id+"F0.wireOp",EDGE,"E35");var subQ15=sQuery(id+"F0.wireOp",EDGE,"E34");var subQ16=sQuery(id+"F0.wireOp",EDGE,"E33");var subQ17=sQuery(id+"F0.wireOp",EDGE,"E32");var subQ18=sQuery(id+"F0.wireOp",EDGE,"E31");var subQ22=sQuery(id+"F0.wireOp",EDGE,"E30");var subQ24=sQuery(id+"F0.wireOp",EDGE,"E29");var subQ26=sQuery(id+"F0.wireOp",EDGE,"E28");var subQ27=sQuery(id+"F0.wireOp",EDGE,"E27");var subQ29=sQuery(id+"F0.wireOp",EDGE,"E26");var subQ30=sQuery(id+"F0.wireOp",EDGE,"E25");var subQ31=sQuery(id+"F0.wireOp",EDGE,"E24");var subQ32=sQuery(id+"F0.wireOp",EDGE,"E23");var subQ33=sQuery(id+"F0.wireOp",EDGE,"E9");var subQ34=sQuery(id+"F0.wireOp",EDGE,"E7");var subQ35=sQuery(id+"F0.wireOp",EDGE,"E6");var subQ36=sQuery(id+"F0.wireOp",EDGE,"E5");var subQ37=sQuery(id+"F0.wireOp",EDGE,"E4");var subQ38=sQuery(id+"F0.wireOp",EDGE,"E10");var subQ39=sQuery(id+"F0.wireOp",EDGE,"E0");var subQ40=sQuery(id+"F0.wireOp",EDGE,"E22");var subQ41=sQuery(id+"F0.wireOp",EDGE,"E3");var subQ42=sQuery(id+"F0.wireOp",EDGE,"E1");var subQ43=sQuery(id+"F0.wireOp",EDGE,"E2");var subQ44=sQuery(id+"F0.wireOp",EDGE,"E11");var subQ45=sQuery(id+"F0.wireOp",EDGE,"E12");var subQ46=sQuery(id+"F0.wireOp",EDGE,"E13");var subQ47=sQuery(id+"F0.wireOp",EDGE,"E14");var subQ48=sQuery(id+"F0.wireOp",EDGE,"E15");var subQ49=sQuery(id+"F0.wireOp",EDGE,"E16");var subQ50=sQuery(id+"F0.wireOp",EDGE,"E17");var subQ51=sQuery(id+"F0.wireOp",EDGE,"E18");var subQ52=sQuery(id+"F0.wireOp",EDGE,"E19");var subQ53=sQuery(id+"F0.wireOp",EDGE,"E20");var subQ54=sQuery(id+"F0.wireOp",EDGE,"E21");var subQ55=sQuery(id+"F0.wireOp",EDGE,"E64");var subQ56=sQuery(id+"F0.wireOp",EDGE,"E61");var subQ57=sQuery(id+"F0.wireOp",EDGE,"E63");var subQ58=sQuery(id+"F0.wireOp",EDGE,"E65");var subQ59=sQuery(id+"F0.wireOp",EDGE,"E67");var subQ60=sQuery(id+"F0.wireOp",EDGE,"E70");var subQ61=sQuery(id+"F0.wireOp",EDGE,"E69");var subQ62=sQuery(id+"F0.wireOp",EDGE,"E71");var subQ63=sQuery(id+"F0.wireOp",EDGE,"E76");var subQ64=sQuery(id+"F0.wireOp",EDGE,"E73");var subQ65=sQuery(id+"F0.wireOp",EDGE,"E75");var subQ66=sQuery(id+"F0.wireOp",EDGE,"E77");var subQ67=sQuery(id+"F0.wireOp",EDGE,"E79");var subQ68=sQuery(id+"F0.wireOp",EDGE,"E80");var subQ69=sQuery(id+"F0.wireOp",EDGE,"E82");var subQ70=sQuery(id+"F0.wireOp",EDGE,"E81");var subQ71=sQuery(id+"F0.wireOp",EDGE,"E83");var subQ72=sQuery(id+"F0.wireOp",EDGE,"E88");var subQ73=sQuery(id+"F0.wireOp",EDGE,"E85");var subQ74=sQuery(id+"F0.wireOp",EDGE,"E87");var subQ75=sQuery(id+"F0.wireOp",EDGE,"E89");var subQ76=sQuery(id+"F0.wireOp",EDGE,"E90");var subQ77=sQuery(id+"F0.wireOp",EDGE,"E91");var subQ78=sQuery(id+"F0.wireOp",EDGE,"E102");var subQ79=sQuery(id+"F0.wireOp",EDGE,"E105");var subQ80=sQuery(id+"F0.wireOp",EDGE,"E108");var subQ81=sQuery(id+"F0.wireOp",EDGE,"E111");var subQ82=sQuery(id+"F0.wireOp",EDGE,"E114");var subQ83=sQuery(id+"F0.wireOp",EDGE,"E117");var subQ84=sQuery(id+"F0.wireOp",EDGE,"E120");var subQ85=sQuery(id+"F0.wireOp",EDGE,"E123");var subQ86=sQuery(id+"F0.wireOp",EDGE,"E126");var subQ87=sQuery(id+"F0.wireOp",EDGE,"E129");var subQ88=sQuery(id+"F0.wireOp",EDGE,"E132");var subQ89=sQuery(id+"F0.wireOp",EDGE,"E135");var subQ90=sQuery(id+"F0.wireOp",EDGE,"E138");var subQ91=sQuery(id+"F0.wireOp",EDGE,"E141");Q0=makeQuery(id+"F3.boolean.opBoolean","SPLIT",FACE,{"disambiguationData":[TD([makeQuery(id+"F1.opExtrude","SWEPT_FACE",FACE,{"disambiguationData":[OSD([subQ39])]})])],"derivedFrom":makeQuery(id+"F1.opExtrude","CAP_FACE",FACE,{"disambiguationData":[OSD([subQ39,subQ42,subQ43,subQ41,subQ37,subQ36,subQ35,subQ34,subQ33,subQ38,subQ44,subQ45,subQ46,subQ47,subQ48,subQ49,subQ50,subQ51,subQ52,subQ53,subQ54,subQ40,subQ32,subQ31,subQ30,subQ29,subQ27,subQ26,subQ24,subQ22,subQ18,subQ17,subQ16,subQ15,subQ14,subQ13,subQ12,subQ11,subQ10,subQ9,subQ8,subQ7,subQ5,subQ6,subQ4,sQuery(id+"F0.wireOp",EDGE,"E54"),subQ3,sQuery(id+"F0.wireOp",EDGE,"E56"),subQ2,subQ1,subQ0,subQ56,subQ57,subQ55,subQ58,sQuery(id+"F0.wireOp",EDGE,"E66"),subQ59,sQuery(id+"F0.wireOp",EDGE,"E68"),subQ61,subQ60,subQ62,subQ64,subQ65,subQ63,subQ66,sQuery(id+"F0.wireOp",EDGE,"E78"),subQ67,subQ68,subQ70,subQ69,subQ71,subQ73,subQ74,subQ72,subQ75,subQ76,subQ77,sQuery(id+"F0.wireOp",EDGE,"E92"),sQuery(id+"F0.wireOp",EDGE,"E93"),subQ78,subQ79,subQ80,subQ81,subQ82,subQ83,subQ84,subQ85,subQ86,subQ87,subQ88,subQ89,subQ90,subQ91,sQuery(id+"F0.wireOp",EDGE,"E144")])],"isStart":true})});}
            var sketch = newSketch(context, id + "F7", { "sketchPlane" : qUnion([Q0])});
            skLineSegment(sketch, "E178.bottom", {"start": v(15.35, -41.6) * mm, "end": v(24.25, -41.6) * mm});
            skLineSegment(sketch, "E178.top", {"start": v(16.8, -52.4) * mm, "end": v(22.8, -52.4) * mm});
            skLineSegment(sketch, "E178.left", {"start": v(15.15, -41.8) * mm, "end": v(15.15, -51.77) * mm});
            skLineSegment(sketch, "E178.right", {"start": v(24.45, -41.8) * mm, "end": v(24.45, -51.77) * mm});
            skLineSegment(sketch, "E179", {"start": v(15.15, -51.77) * mm, "end": v(16.8, -52.4) * mm});
            skLineSegment(sketch, "E180", {"start": v(22.8, -52.4) * mm, "end": v(24.45, -51.77) * mm});
            skArc(sketch, "E181", {"start": v(15.35, -41.6) * mm, "mid": v(15, -41.46) * mm, "end": v(15.15, -41.8) * mm});
            skArc(sketch, "E182", {"start": v(24.45, -41.8) * mm, "mid": v(24.6, -41.46) * mm, "end": v(24.25, -41.6) * mm});
            skCircle(sketch, "E183.0", {"center": v(19.8, -47.25) * mm, "radius": 4.05 * mm});
            skPoint(sketch, "E184", {"position": v(19.8, -52.4) * mm});
            skLineSegment(sketch, "E185.0.1.0", {"start": v(16.8, -37.4) * mm, "end": v(22.8, -37.4) * mm});
            skPoint(sketch, "E185.0.1.1", {"position": v(19.8, -32.25) * mm});
            skLineSegment(sketch, "E185.0.1.2", {"start": v(22.8, -37.4) * mm, "end": v(24.45, -36.77) * mm});
            skLineSegment(sketch, "E185.0.1.3", {"start": v(15.15, -36.77) * mm, "end": v(16.8, -37.4) * mm});
            skLineSegment(sketch, "E185.0.1.4", {"start": v(24.45, -26.8) * mm, "end": v(24.45, -36.77) * mm});
            skLineSegment(sketch, "E185.0.1.5", {"start": v(15.15, -26.8) * mm, "end": v(15.15, -36.77) * mm});
            skCircle(sketch, "E185.0.1.6", {"center": v(19.8, -32.25) * mm, "radius": 4.05 * mm});
            skLineSegment(sketch, "E185.0.1.7", {"start": v(15.35, -26.6) * mm, "end": v(24.25, -26.6) * mm});
            skPoint(sketch, "E185.0.1.8", {"position": v(19.8, -37.4) * mm});
            skArc(sketch, "E185.0.1.9", {"start": v(15.35, -26.6) * mm, "mid": v(15, -26.46) * mm, "end": v(15.15, -26.8) * mm});
            skArc(sketch, "E185.0.1.10", {"start": v(24.45, -26.8) * mm, "mid": v(24.6, -26.46) * mm, "end": v(24.25, -26.6) * mm});
            skLineSegment(sketch, "E185.0.2.0", {"start": v(16.8, -22.4) * mm, "end": v(22.8, -22.4) * mm, "construction": true});
            skPoint(sketch, "E185.0.2.1", {"position": v(19.8, -17.25) * mm});
            skLineSegment(sketch, "E185.0.2.2", {"start": v(22.8, -22.4) * mm, "end": v(24.45, -21.77) * mm, "construction": true});
            skLineSegment(sketch, "E185.0.2.3", {"start": v(15.15, -21.77) * mm, "end": v(16.8, -22.4) * mm, "construction": true});
            skLineSegment(sketch, "E185.0.2.4", {"start": v(24.45, -11.8) * mm, "end": v(24.45, -21.77) * mm, "construction": true});
            skLineSegment(sketch, "E185.0.2.5", {"start": v(15.15, -11.8) * mm, "end": v(15.15, -21.77) * mm, "construction": true});
            skCircle(sketch, "E185.0.2.6", {"center": v(19.8, -17.25) * mm, "radius": 4.05 * mm, "construction": true});
            skLineSegment(sketch, "E185.0.2.7", {"start": v(15.35, -11.6) * mm, "end": v(24.25, -11.6) * mm, "construction": true});
            skPoint(sketch, "E185.0.2.8", {"position": v(19.8, -22.4) * mm});
            skArc(sketch, "E185.0.2.9", {"start": v(15.35, -11.6) * mm, "mid": v(15, -11.46) * mm, "end": v(15.15, -11.8) * mm, "construction": true});
            skArc(sketch, "E185.0.2.10", {"start": v(24.45, -11.8) * mm, "mid": v(24.6, -11.46) * mm, "end": v(24.25, -11.6) * mm, "construction": true});
            skLineSegment(sketch, "E185.1.0.0", {"start": v(4.1, -52.4) * mm, "end": v(10.1, -52.4) * mm});
            skPoint(sketch, "E185.1.0.1", {"position": v(7.1, -47.25) * mm});
            skLineSegment(sketch, "E185.1.0.2", {"start": v(10.1, -52.4) * mm, "end": v(11.75, -51.77) * mm});
            skLineSegment(sketch, "E185.1.0.3", {"start": v(2.45, -51.77) * mm, "end": v(4.1, -52.4) * mm});
            skLineSegment(sketch, "E185.1.0.4", {"start": v(11.75, -41.8) * mm, "end": v(11.75, -51.77) * mm});
            skLineSegment(sketch, "E185.1.0.5", {"start": v(2.45, -41.8) * mm, "end": v(2.45, -51.77) * mm});
            skCircle(sketch, "E185.1.0.6", {"center": v(7.1, -47.25) * mm, "radius": 4.05 * mm});
            skLineSegment(sketch, "E185.1.0.7", {"start": v(2.65, -41.6) * mm, "end": v(11.55, -41.6) * mm});
            skPoint(sketch, "E185.1.0.8", {"position": v(7.1, -52.4) * mm});
            skArc(sketch, "E185.1.0.9", {"start": v(2.65, -41.6) * mm, "mid": v(2.3, -41.46) * mm, "end": v(2.45, -41.8) * mm});
            skArc(sketch, "E185.1.0.10", {"start": v(11.75, -41.8) * mm, "mid": v(11.9, -41.46) * mm, "end": v(11.55, -41.6) * mm});
            skLineSegment(sketch, "E185.1.1.0", {"start": v(4.1, -37.4) * mm, "end": v(10.1, -37.4) * mm});
            skPoint(sketch, "E185.1.1.1", {"position": v(7.1, -32.25) * mm});
            skLineSegment(sketch, "E185.1.1.2", {"start": v(10.1, -37.4) * mm, "end": v(11.75, -36.77) * mm});
            skLineSegment(sketch, "E185.1.1.3", {"start": v(2.45, -36.77) * mm, "end": v(4.1, -37.4) * mm});
            skLineSegment(sketch, "E185.1.1.4", {"start": v(11.75, -26.8) * mm, "end": v(11.75, -36.77) * mm});
            skLineSegment(sketch, "E185.1.1.5", {"start": v(2.45, -26.8) * mm, "end": v(2.45, -36.77) * mm});
            skCircle(sketch, "E185.1.1.6", {"center": v(7.1, -32.25) * mm, "radius": 4.05 * mm});
            skLineSegment(sketch, "E185.1.1.7", {"start": v(2.65, -26.6) * mm, "end": v(11.55, -26.6) * mm});
            skPoint(sketch, "E185.1.1.8", {"position": v(7.1, -37.4) * mm});
            skArc(sketch, "E185.1.1.9", {"start": v(2.65, -26.6) * mm, "mid": v(2.3, -26.46) * mm, "end": v(2.45, -26.8) * mm});
            skArc(sketch, "E185.1.1.10", {"start": v(11.75, -26.8) * mm, "mid": v(11.9, -26.46) * mm, "end": v(11.55, -26.6) * mm});
            skLineSegment(sketch, "E185.1.2.0", {"start": v(4.1, -22.4) * mm, "end": v(10.1, -22.4) * mm});
            skPoint(sketch, "E185.1.2.1", {"position": v(7.1, -17.25) * mm});
            skLineSegment(sketch, "E185.1.2.2", {"start": v(10.1, -22.4) * mm, "end": v(11.75, -21.77) * mm});
            skLineSegment(sketch, "E185.1.2.3", {"start": v(2.45, -21.77) * mm, "end": v(4.1, -22.4) * mm});
            skLineSegment(sketch, "E185.1.2.4", {"start": v(11.75, -11.8) * mm, "end": v(11.75, -21.77) * mm});
            skLineSegment(sketch, "E185.1.2.5", {"start": v(2.45, -11.8) * mm, "end": v(2.45, -21.77) * mm});
            skCircle(sketch, "E185.1.2.6", {"center": v(7.1, -17.25) * mm, "radius": 4.05 * mm});
            skLineSegment(sketch, "E185.1.2.7", {"start": v(2.65, -11.6) * mm, "end": v(11.55, -11.6) * mm});
            skPoint(sketch, "E185.1.2.8", {"position": v(7.1, -22.4) * mm});
            skArc(sketch, "E185.1.2.9", {"start": v(2.65, -11.6) * mm, "mid": v(2.3, -11.46) * mm, "end": v(2.45, -11.8) * mm});
            skArc(sketch, "E185.1.2.10", {"start": v(11.75, -11.8) * mm, "mid": v(11.9, -11.46) * mm, "end": v(11.55, -11.6) * mm});
            skLineSegment(sketch, "E185.direction1", {"start": v(15.15, -51.77) * mm, "end": v(2.45, -51.77) * mm, "construction": true});
            skLineSegment(sketch, "E185.direction2", {"start": v(15.15, -51.77) * mm, "end": v(15.15, -36.77) * mm, "construction": true});
            skLineSegment(sketch, "E186", {"start": v(0, -56.75) * mm, "end": v(0, 64.25) * mm, "construction": true});
            skLineSegment(sketch, "E187", {"start": v(30.3, -56.75) * mm, "end": v(30.3, -24.27) * mm});
            skLineSegment(sketch, "E188", {"start": v(30.3, -24.27) * mm, "end": v(14.25, -24.27) * mm});
            skLineSegment(sketch, "E189", {"start": v(14.25, -24.27) * mm, "end": v(14.25, -9.1) * mm});
            skLineSegment(sketch, "E190", {"start": v(14.25, -9.1) * mm, "end": v(0, -9.1) * mm});
            skLineSegment(sketch, "E191", {"start": v(0, -9.1) * mm, "end": v(0, -56.75) * mm});
            skLineSegment(sketch, "E192", {"start": v(0, -56.75) * mm, "end": v(30.3, -56.75) * mm});
            skPoint(sketch, "E193.orphan", {"position": v(0, -64.25) * mm});
            skPoint(sketch, "E194", {"position": v(19.8, -41.6) * mm});
            skLineSegment(sketch, "E195", {"start": v(19.8, -41.6) * mm, "end": v(19.8, -52.4) * mm, "construction": true});
            skSolve(sketch);
        }
        {
            var Q0;
            Q0 = qSketchRegion(id + "F7", true);
            extrude(context, id + "F8", {"entities" : qUnion([Q0]), "operationType" : NewBodyOperationType.ADD, "depth" : 11 * mm, "offsetDistance" : 25 * mm});
        }
        {
            var Q0;
            Q0=makeQuery(id+"F8.opExtrude","CAP_EDGE",EDGE,{"disambiguationData":[OSD([sQuery(id+"F7.wireOp",EDGE,"E185.1.2.5")])],"isStart":false});
            var Q1;
            Q1=makeQuery(id+"F8.opExtrude","CAP_EDGE",EDGE,{"disambiguationData":[OSD([sQuery(id+"F7.wireOp",EDGE,"E185.1.2.9")])],"isStart":false});
            var Q2;
            Q2=makeQuery(id+"F8.opExtrude","CAP_EDGE",EDGE,{"disambiguationData":[OSD([sQuery(id+"F7.wireOp",EDGE,"E185.1.2.7")])],"isStart":false});
            var Q3;
            Q3=makeQuery(id+"F8.opExtrude","CAP_EDGE",EDGE,{"disambiguationData":[OSD([sQuery(id+"F7.wireOp",EDGE,"E185.1.2.10")])],"isStart":false});
            var Q4;
            Q4=makeQuery(id+"F8.opExtrude","CAP_EDGE",EDGE,{"disambiguationData":[OSD([sQuery(id+"F7.wireOp",EDGE,"E185.1.2.4")])],"isStart":false});
            var Q5;
            Q5=makeQuery(id+"F8.opExtrude","CAP_EDGE",EDGE,{"disambiguationData":[OSD([sQuery(id+"F7.wireOp",EDGE,"E185.1.2.2")])],"isStart":false});
            var Q6;
            Q6=makeQuery(id+"F8.opExtrude","CAP_EDGE",EDGE,{"disambiguationData":[OSD([sQuery(id+"F7.wireOp",EDGE,"E185.1.2.0")])],"isStart":false});
            var Q7;
            Q7=makeQuery(id+"F8.opExtrude","CAP_EDGE",EDGE,{"disambiguationData":[OSD([sQuery(id+"F7.wireOp",EDGE,"E185.1.2.3")])],"isStart":false});
            var Q8;
            Q8=makeQuery(id+"F8.opExtrude","CAP_EDGE",EDGE,{"disambiguationData":[OSD([sQuery(id+"F7.wireOp",EDGE,"E185.1.1.7")])],"isStart":false});
            var Q9;
            Q9=makeQuery(id+"F8.opExtrude","CAP_EDGE",EDGE,{"disambiguationData":[OSD([sQuery(id+"F7.wireOp",EDGE,"E185.1.1.9")])],"isStart":false});
            var Q10;
            Q10=makeQuery(id+"F8.opExtrude","CAP_EDGE",EDGE,{"disambiguationData":[OSD([sQuery(id+"F7.wireOp",EDGE,"E185.1.1.5")])],"isStart":false});
            var Q11;
            Q11=makeQuery(id+"F8.opExtrude","CAP_EDGE",EDGE,{"disambiguationData":[OSD([sQuery(id+"F7.wireOp",EDGE,"E185.1.1.3")])],"isStart":false});
            var Q12;
            Q12=makeQuery(id+"F8.opExtrude","CAP_EDGE",EDGE,{"disambiguationData":[OSD([sQuery(id+"F7.wireOp",EDGE,"E185.1.1.0")])],"isStart":false});
            var Q13;
            Q13=makeQuery(id+"F8.opExtrude","CAP_EDGE",EDGE,{"disambiguationData":[OSD([sQuery(id+"F7.wireOp",EDGE,"E185.1.1.2")])],"isStart":false});
            var Q14;
            Q14=makeQuery(id+"F8.opExtrude","CAP_EDGE",EDGE,{"disambiguationData":[OSD([sQuery(id+"F7.wireOp",EDGE,"E185.1.1.4")])],"isStart":false});
            var Q15;
            Q15=makeQuery(id+"F8.opExtrude","CAP_EDGE",EDGE,{"disambiguationData":[OSD([sQuery(id+"F7.wireOp",EDGE,"E185.1.1.10")])],"isStart":false});
            var Q16;
            Q16=makeQuery(id+"F8.opExtrude","CAP_EDGE",EDGE,{"disambiguationData":[OSD([sQuery(id+"F7.wireOp",EDGE,"E185.0.1.9")])],"isStart":false});
            var Q17;
            Q17=makeQuery(id+"F8.opExtrude","CAP_EDGE",EDGE,{"disambiguationData":[OSD([sQuery(id+"F7.wireOp",EDGE,"E185.0.1.5")])],"isStart":false});
            var Q18;
            Q18=makeQuery(id+"F8.opExtrude","CAP_EDGE",EDGE,{"disambiguationData":[OSD([sQuery(id+"F7.wireOp",EDGE,"E185.0.1.7")])],"isStart":false});
            var Q19;
            Q19=makeQuery(id+"F8.opExtrude","CAP_EDGE",EDGE,{"disambiguationData":[OSD([sQuery(id+"F7.wireOp",EDGE,"E185.0.1.10")])],"isStart":false});
            var Q20;
            Q20=makeQuery(id+"F8.opExtrude","CAP_EDGE",EDGE,{"disambiguationData":[OSD([sQuery(id+"F7.wireOp",EDGE,"E185.0.1.4")])],"isStart":false});
            var Q21;
            Q21=makeQuery(id+"F8.opExtrude","CAP_EDGE",EDGE,{"disambiguationData":[OSD([sQuery(id+"F7.wireOp",EDGE,"E185.0.1.2")])],"isStart":false});
            var Q22;
            Q22=makeQuery(id+"F8.opExtrude","CAP_EDGE",EDGE,{"disambiguationData":[OSD([sQuery(id+"F7.wireOp",EDGE,"E185.0.1.0")])],"isStart":false});
            var Q23;
            Q23=makeQuery(id+"F8.opExtrude","CAP_EDGE",EDGE,{"disambiguationData":[OSD([sQuery(id+"F7.wireOp",EDGE,"E185.0.1.3")])],"isStart":false});
            var Q24;
            Q24=makeQuery(id+"F8.opExtrude","CAP_EDGE",EDGE,{"disambiguationData":[OSD([sQuery(id+"F7.wireOp",EDGE,"E185.1.0.5")])],"isStart":false});
            var Q25;
            Q25=makeQuery(id+"F8.opExtrude","CAP_EDGE",EDGE,{"disambiguationData":[OSD([sQuery(id+"F7.wireOp",EDGE,"E185.1.0.9")])],"isStart":false});
            var Q26;
            Q26=makeQuery(id+"F8.opExtrude","CAP_EDGE",EDGE,{"disambiguationData":[OSD([sQuery(id+"F7.wireOp",EDGE,"E185.1.0.7")])],"isStart":false});
            var Q27;
            Q27=makeQuery(id+"F8.opExtrude","CAP_EDGE",EDGE,{"disambiguationData":[OSD([sQuery(id+"F7.wireOp",EDGE,"E185.1.0.10")])],"isStart":false});
            var Q28;
            Q28=makeQuery(id+"F8.opExtrude","CAP_EDGE",EDGE,{"disambiguationData":[OSD([sQuery(id+"F7.wireOp",EDGE,"E185.1.0.4")])],"isStart":false});
            var Q29;
            Q29=makeQuery(id+"F8.opExtrude","CAP_EDGE",EDGE,{"disambiguationData":[OSD([sQuery(id+"F7.wireOp",EDGE,"E185.1.0.2")])],"isStart":false});
            var Q30;
            Q30=makeQuery(id+"F8.opExtrude","CAP_EDGE",EDGE,{"disambiguationData":[OSD([sQuery(id+"F7.wireOp",EDGE,"E185.1.0.0")])],"isStart":false});
            var Q31;
            Q31=makeQuery(id+"F8.opExtrude","CAP_EDGE",EDGE,{"disambiguationData":[OSD([sQuery(id+"F7.wireOp",EDGE,"E185.1.0.3")])],"isStart":false});
            var Q32;
            Q32=makeQuery(id+"F8.opExtrude","CAP_EDGE",EDGE,{"disambiguationData":[OSD([sQuery(id+"F7.wireOp",EDGE,"E178.bottom")])],"isStart":false});
            var Q33;
            Q33=makeQuery(id+"F8.opExtrude","CAP_EDGE",EDGE,{"disambiguationData":[OSD([sQuery(id+"F7.wireOp",EDGE,"E181")])],"isStart":false});
            var Q34;
            Q34=makeQuery(id+"F8.opExtrude","CAP_EDGE",EDGE,{"disambiguationData":[OSD([sQuery(id+"F7.wireOp",EDGE,"E178.left")])],"isStart":false});
            var Q35;
            Q35=makeQuery(id+"F8.opExtrude","CAP_EDGE",EDGE,{"disambiguationData":[OSD([sQuery(id+"F7.wireOp",EDGE,"E179")])],"isStart":false});
            var Q36;
            Q36=makeQuery(id+"F8.opExtrude","CAP_EDGE",EDGE,{"disambiguationData":[OSD([sQuery(id+"F7.wireOp",EDGE,"E178.top")])],"isStart":false});
            var Q37;
            Q37=makeQuery(id+"F8.opExtrude","CAP_EDGE",EDGE,{"disambiguationData":[OSD([sQuery(id+"F7.wireOp",EDGE,"E180")])],"isStart":false});
            var Q38;
            Q38=makeQuery(id+"F8.opExtrude","CAP_EDGE",EDGE,{"disambiguationData":[OSD([sQuery(id+"F7.wireOp",EDGE,"E178.right")])],"isStart":false});
            var Q39;
            Q39=makeQuery(id+"F8.opExtrude","CAP_EDGE",EDGE,{"disambiguationData":[OSD([sQuery(id+"F7.wireOp",EDGE,"E182")])],"isStart":false});
            chamfer(context, id + "F9", {"entities" : qUnion([Q0, Q1, Q2, Q3, Q4, Q5, Q6, Q7, Q8, Q9, Q10, Q11, Q12, Q13, Q14, Q15, Q16, Q17, Q18, Q19, Q20, Q21, Q22, Q23, Q24, Q25, Q26, Q27, Q28, Q29, Q30, Q31, Q32, Q33, Q34, Q35, Q36, Q37, Q38, Q39]), "chamferType" : ChamferType.OFFSET_ANGLE, "width" : 5 * mm, "oppositeDirection" : false, "angle" : 8 * degree, "tangentPropagation" : true});
        }
        {
            var Q0;
            {var subQ0=sQuery(id+"F0.wireOp",EDGE,"E91");var subQ2=sQuery(id+"F0.wireOp",EDGE,"E90");var subQ4=sQuery(id+"F0.wireOp",EDGE,"E82");var subQ5=sQuery(id+"F0.wireOp",EDGE,"E81");var subQ7=sQuery(id+"F0.wireOp",EDGE,"E80");var subQ9=sQuery(id+"F0.wireOp",EDGE,"E79");var subQ11=sQuery(id+"F0.wireOp",EDGE,"E75");var subQ13=sQuery(id+"F0.wireOp",EDGE,"E65");var subQ16=sQuery(id+"F0.wireOp",EDGE,"E63");var subQ18=sQuery(id+"F0.wireOp",EDGE,"E64");var subQ19=sQuery(id+"F0.wireOp",EDGE,"E61");var subQ21=sQuery(id+"F0.wireOp",EDGE,"E59");var subQ24=sQuery(id+"F0.wireOp",EDGE,"E58");var subQ25=sQuery(id+"F0.wireOp",EDGE,"E57");var subQ27=sQuery(id+"F0.wireOp",EDGE,"E55");var subQ29=sQuery(id+"F0.wireOp",EDGE,"E53");var subQ31=sQuery(id+"F0.wireOp",EDGE,"E51");var subQ33=sQuery(id+"F0.wireOp",EDGE,"E77");var subQ35=sQuery(id+"F0.wireOp",EDGE,"E12");var subQ37=sQuery(id+"F0.wireOp",EDGE,"E35");var subQ40=sQuery(id+"F0.wireOp",EDGE,"E76");var subQ41=sQuery(id+"F0.wireOp",EDGE,"E73");var subQ43=sQuery(id+"F0.wireOp",EDGE,"E10");var subQ45=sQuery(id+"F0.wireOp",EDGE,"E33");var subQ47=sQuery(id+"F0.wireOp",EDGE,"E108");var subQ49=sQuery(id+"F0.wireOp",EDGE,"E71");var subQ51=sQuery(id+"F0.wireOp",EDGE,"E9");var subQ53=sQuery(id+"F0.wireOp",EDGE,"E4");var subQ54=makeQuery(id+"F1.opExtrude","SWEPT_FACE",FACE,{"disambiguationData":[OSD([subQ53])]});var subQ55=sQuery(id+"F0.wireOp",EDGE,"E28");var subQ57=sQuery(id+"F0.wireOp",EDGE,"E83");var subQ59=sQuery(id+"F0.wireOp",EDGE,"E17");var subQ63=sQuery(id+"F0.wireOp",EDGE,"E47");var subQ65=sQuery(id+"F0.wireOp",EDGE,"E67");var subQ67=sQuery(id+"F0.wireOp",EDGE,"E5");var subQ69=sQuery(id+"F0.wireOp",EDGE,"E88");var subQ70=sQuery(id+"F0.wireOp",EDGE,"E85");var subQ72=sQuery(id+"F0.wireOp",EDGE,"E18");var subQ76=sQuery(id+"F0.wireOp",EDGE,"E52");var subQ77=sQuery(id+"F0.wireOp",EDGE,"E49");var subQ79=sQuery(id+"F0.wireOp",EDGE,"E6");var subQ81=sQuery(id+"F0.wireOp",EDGE,"E87");var subQ83=sQuery(id+"F0.wireOp",EDGE,"E19");var subQ87=sQuery(id+"F0.wireOp",EDGE,"E70");var subQ88=sQuery(id+"F0.wireOp",EDGE,"E69");var subQ90=sQuery(id+"F0.wireOp",EDGE,"E7");var subQ92=sQuery(id+"F0.wireOp",EDGE,"E89");var subQ94=sQuery(id+"F0.wireOp",EDGE,"E20");var subQ97=sQuery(id+"F0.wireOp",EDGE,"E25");var subQ99=sQuery(id+"F0.wireOp",EDGE,"E26");var subQ103=sQuery(id+"F0.wireOp",EDGE,"E27");var subQ105=sQuery(id+"F0.wireOp",EDGE,"E34");var subQ107=sQuery(id+"F0.wireOp",EDGE,"E111");var subQ110=sQuery(id+"F0.wireOp",EDGE,"E36");var subQ112=sQuery(id+"F0.wireOp",EDGE,"E46");var subQ113=sQuery(id+"F0.wireOp",EDGE,"E45");var subQ120=sQuery(id+"F0.wireOp",EDGE,"E41");var subQ124=sQuery(id+"F0.wireOp",EDGE,"E44");var subQ130=sQuery(id+"F0.wireOp",EDGE,"E102");var subQ133=sQuery(id+"F0.wireOp",EDGE,"E105");var subQ136=sQuery(id+"F0.wireOp",EDGE,"E126");var subQ137=sQuery(id+"F0.wireOp",EDGE,"E117");var subQ138=sQuery(id+"F0.wireOp",EDGE,"E114");var subQ139=sQuery(id+"F0.wireOp",EDGE,"E32");var subQ141=sQuery(id+"F0.wireOp",EDGE,"E31");var subQ143=sQuery(id+"F0.wireOp",EDGE,"E30");var subQ145=sQuery(id+"F0.wireOp",EDGE,"E29");var subQ147=sQuery(id+"F0.wireOp",EDGE,"E24");var subQ149=sQuery(id+"F0.wireOp",EDGE,"E23");var subQ151=sQuery(id+"F0.wireOp",EDGE,"E0");var subQ152=makeQuery(id+"F1.opExtrude","SWEPT_FACE",FACE,{"disambiguationData":[OSD([subQ151])]});var subQ153=sQuery(id+"F0.wireOp",EDGE,"E22");var subQ155=sQuery(id+"F0.wireOp",EDGE,"E3");var subQ157=sQuery(id+"F0.wireOp",EDGE,"E1");var subQ159=sQuery(id+"F0.wireOp",EDGE,"E2");var subQ161=sQuery(id+"F0.wireOp",EDGE,"E11");var subQ163=sQuery(id+"F0.wireOp",EDGE,"E13");var subQ165=sQuery(id+"F0.wireOp",EDGE,"E14");var subQ167=sQuery(id+"F0.wireOp",EDGE,"E15");var subQ169=sQuery(id+"F0.wireOp",EDGE,"E16");var subQ171=sQuery(id+"F0.wireOp",EDGE,"E21");var subQ173=sQuery(id+"F0.wireOp",EDGE,"E120");var subQ174=sQuery(id+"F0.wireOp",EDGE,"E123");var subQ175=sQuery(id+"F0.wireOp",EDGE,"E129");var subQ176=sQuery(id+"F0.wireOp",EDGE,"E132");var subQ177=sQuery(id+"F0.wireOp",EDGE,"E135");var subQ178=sQuery(id+"F0.wireOp",EDGE,"E138");var subQ179=sQuery(id+"F0.wireOp",EDGE,"E141");Q0=makeQuery(id+"FAJUFp0u1zRX4jL_1.1.F8.boolean.opBoolean","SPLIT",FACE,{"disambiguationData":[TD([subQ54])],"derivedFrom":makeQuery(id+"F8.boolean.opBoolean","SPLIT",FACE,{"disambiguationData":[TD([subQ152])],"derivedFrom":makeQuery(id+"F3.boolean.opBoolean","SPLIT",FACE,{"disambiguationData":[TD([subQ152])],"derivedFrom":makeQuery(id+"F1.opExtrude","CAP_FACE",FACE,{"disambiguationData":[OSD([subQ151,subQ157,subQ159,subQ155,subQ53,subQ67,subQ79,subQ90,subQ51,subQ43,subQ161,subQ35,subQ163,subQ165,subQ167,subQ169,subQ59,subQ72,subQ83,subQ94,subQ171,subQ153,subQ149,subQ147,subQ97,subQ99,subQ103,subQ55,subQ145,subQ143,subQ141,subQ139,subQ45,subQ105,subQ37,subQ110,subQ120,subQ124,subQ113,subQ112,subQ63,subQ77,subQ31,subQ76,subQ29,sQuery(id+"F0.wireOp",EDGE,"E54"),subQ27,sQuery(id+"F0.wireOp",EDGE,"E56"),subQ25,subQ24,subQ21,subQ19,subQ16,subQ18,subQ13,sQuery(id+"F0.wireOp",EDGE,"E66"),subQ65,sQuery(id+"F0.wireOp",EDGE,"E68"),subQ88,subQ87,subQ49,subQ41,subQ11,subQ40,subQ33,sQuery(id+"F0.wireOp",EDGE,"E78"),subQ9,subQ7,subQ5,subQ4,subQ57,subQ70,subQ81,subQ69,subQ92,subQ2,subQ0,sQuery(id+"F0.wireOp",EDGE,"E92"),sQuery(id+"F0.wireOp",EDGE,"E93"),subQ130,subQ133,subQ47,subQ107,subQ138,subQ137,subQ173,subQ174,subQ136,subQ175,subQ176,subQ177,subQ178,subQ179,sQuery(id+"F0.wireOp",EDGE,"E144")])],"isStart":true})})})});}
            var sketch = newSketch(context, id + "F10", { "sketchPlane" : qUnion([Q0])});
            skLineSegment(sketch, "E196", {"start": v(30.3, -24.27) * mm, "end": v(30.3, 54.25) * mm});
            skLineSegment(sketch, "E197", {"start": v(30.3, 54.25) * mm, "end": v(27.51, 54.25) * mm});
            skLineSegment(sketch, "E198", {"start": v(27.51, 54.25) * mm, "end": v(27.51, 5.71) * mm});
            skLineSegment(sketch, "E199", {"start": v(27.51, -24.27) * mm, "end": v(30.3, -24.27) * mm});
            skLineSegment(sketch, "E200.0", {"start": v(27.51, 49.25) * mm, "end": v(-27.51, 49.25) * mm, "construction": true});
            skLineSegment(sketch, "E201", {"start": v(0, -9.1) * mm, "end": v(0, 49.25) * mm});
            skLineSegment(sketch, "E202", {"start": v(0, 49.25) * mm, "end": v(1.7, 49.25) * mm});
            skLineSegment(sketch, "E203", {"start": v(1.7, 49.25) * mm, "end": v(1.7, -9.1) * mm});
            skLineSegment(sketch, "E204", {"start": v(1.7, -9.1) * mm, "end": v(0, -9.1) * mm});
            skLineSegment(sketch, "E205.bottom", {"start": v(27.51, 5.71) * mm, "end": v(14.25, 5.71) * mm});
            skLineSegment(sketch, "E205.top", {"start": v(27.51, -9.71) * mm, "end": v(14.25, -9.71) * mm});
            skLineSegment(sketch, "E205.right", {"start": v(14.25, 5.71) * mm, "end": v(14.25, -9.71) * mm});
            skLineSegment(sketch, "E206", {"start": v(14.25, -2) * mm, "end": v(27.51, -2) * mm, "construction": true});
            skLineSegment(sketch, "E207.trimOffspring", {"start": v(27.51, -9.71) * mm, "end": v(27.51, -24.27) * mm});
            skPoint(sketch, "E208", {"position": v(20.55, -2) * mm});
            skCircle(sketch, "E209.0", {"center": v(20.55, -2) * mm, "radius": 3.45 * mm});
            skSolve(sketch);
        }
        {
            var Q0;
            Q0 = qSketchRegion(id + "F10", true);
            extrude(context, id + "F11", {"entities" : qUnion([Q0]), "operationType" : NewBodyOperationType.ADD, "depth" : 2.8 * mm, "offsetDistance" : 25 * mm});
        }
        {
            var Q0;
            {var subQ0=sQuery(id+"F7.wireOp",EDGE,"E192");var subQ1=sQuery(id+"F7.wireOp",EDGE,"E191");var subQ2=sQuery(id+"F7.wireOp",EDGE,"E190");var subQ3=sQuery(id+"F7.wireOp",EDGE,"E189");var subQ4=sQuery(id+"F7.wireOp",EDGE,"E188");var subQ5=sQuery(id+"F7.wireOp",EDGE,"E187");var subQ6=sQuery(id+"F7.wireOp",EDGE,"E185.1.2.10");var subQ7=sQuery(id+"F7.wireOp",EDGE,"E185.1.2.9");var subQ8=sQuery(id+"F7.wireOp",EDGE,"E185.1.2.7");var subQ9=sQuery(id+"F7.wireOp",EDGE,"E185.1.2.5");var subQ10=sQuery(id+"F7.wireOp",EDGE,"E185.1.2.4");var subQ11=sQuery(id+"F7.wireOp",EDGE,"E185.1.2.3");var subQ12=sQuery(id+"F7.wireOp",EDGE,"E185.1.2.2");var subQ13=sQuery(id+"F7.wireOp",EDGE,"E185.1.2.0");var subQ14=sQuery(id+"F7.wireOp",EDGE,"E185.1.1.10");var subQ15=sQuery(id+"F7.wireOp",EDGE,"E185.1.1.9");var subQ16=sQuery(id+"F7.wireOp",EDGE,"E185.1.1.7");var subQ17=sQuery(id+"F7.wireOp",EDGE,"E185.1.1.5");var subQ18=sQuery(id+"F7.wireOp",EDGE,"E185.1.1.4");var subQ19=sQuery(id+"F7.wireOp",EDGE,"E185.1.1.3");var subQ20=sQuery(id+"F7.wireOp",EDGE,"E185.1.1.2");var subQ21=sQuery(id+"F7.wireOp",EDGE,"E185.1.1.0");var subQ22=sQuery(id+"F7.wireOp",EDGE,"E185.1.0.10");var subQ23=sQuery(id+"F7.wireOp",EDGE,"E185.1.0.9");var subQ24=sQuery(id+"F7.wireOp",EDGE,"E185.1.0.7");var subQ25=sQuery(id+"F7.wireOp",EDGE,"E185.1.0.5");var subQ26=sQuery(id+"F7.wireOp",EDGE,"E185.1.0.4");var subQ27=sQuery(id+"F7.wireOp",EDGE,"E185.1.0.3");var subQ28=sQuery(id+"F7.wireOp",EDGE,"E185.1.0.2");var subQ29=sQuery(id+"F7.wireOp",EDGE,"E185.1.0.0");var subQ30=sQuery(id+"F7.wireOp",EDGE,"E185.0.1.10");var subQ31=sQuery(id+"F7.wireOp",EDGE,"E185.0.1.9");var subQ32=sQuery(id+"F7.wireOp",EDGE,"E185.0.1.7");var subQ33=sQuery(id+"F7.wireOp",EDGE,"E185.0.1.5");var subQ34=sQuery(id+"F7.wireOp",EDGE,"E185.0.1.4");var subQ35=sQuery(id+"F7.wireOp",EDGE,"E185.0.1.3");var subQ36=sQuery(id+"F7.wireOp",EDGE,"E185.0.1.2");var subQ37=sQuery(id+"F7.wireOp",EDGE,"E185.0.1.0");var subQ38=sQuery(id+"F7.wireOp",EDGE,"E182");var subQ39=sQuery(id+"F7.wireOp",EDGE,"E181");var subQ40=sQuery(id+"F7.wireOp",EDGE,"E180");var subQ41=sQuery(id+"F7.wireOp",EDGE,"E179");var subQ42=sQuery(id+"F7.wireOp",EDGE,"E178.right");var subQ43=sQuery(id+"F7.wireOp",EDGE,"E178.left");var subQ44=sQuery(id+"F7.wireOp",EDGE,"E178.top");var subQ45=sQuery(id+"F7.wireOp",EDGE,"E178.bottom");Q0=makeQuery(id+"FAJUFp0u1zRX4jL_1.1.F8.boolean.opBoolean","MERGE",FACE,{"derivedFrom":[makeQuery(id+"F8.opExtrude","CAP_FACE",FACE,{"disambiguationData":[OSD([subQ45,subQ44,subQ43,subQ42,subQ41,subQ40,subQ39,subQ38,subQ37,subQ36,subQ35,subQ34,subQ33,subQ32,subQ31,subQ30,subQ29,subQ28,subQ27,subQ26,subQ25,subQ24,subQ23,subQ22,subQ21,subQ20,subQ19,subQ18,subQ17,subQ16,subQ15,subQ14,subQ13,subQ12,subQ11,subQ10,subQ9,subQ8,subQ7,subQ6,subQ5,subQ4,subQ3,subQ2,subQ1,subQ0])],"isStart":false}),makeQuery(id+"FAJUFp0u1zRX4jL_1.1.F8.opExtrude","CAP_FACE",FACE,{"disambiguationData":[OSD([subQ45,subQ44,subQ43,subQ42,subQ41,subQ40,subQ39,subQ38,subQ37,subQ36,subQ35,subQ34,subQ33,subQ32,subQ31,subQ30,subQ29,subQ28,subQ27,subQ26,subQ25,subQ24,subQ23,subQ22,subQ21,subQ20,subQ19,subQ18,subQ17,subQ16,subQ15,subQ14,subQ13,subQ12,subQ11,subQ10,subQ9,subQ8,subQ7,subQ6,subQ5,subQ4,subQ3,subQ2,subQ1,subQ0])],"isStart":false})]});}
            var sketch = newSketch(context, id + "F12", { "sketchPlane" : qUnion([Q0])});
            skPoint(sketch, "E210.0", {"position": v(13.2, -9.5) * mm});
            skPoint(sketch, "E211.0", {"position": v(13.8, -22.75) * mm});
            skCircle(sketch, "E212", {"center": v(13.2, -9.5) * mm, "radius": 2.8 * mm});
            skCircle(sketch, "E213", {"center": v(13.8, -22.75) * mm, "radius": 2.8 * mm});
            skSolve(sketch);
        }
        {
            var Q0;
            Q0 = qSketchRegion(id + "F12", true);
            var Q1;
            {var subQ0=sQuery(id+"F0.wireOp",EDGE,"E89");var subQ2=sQuery(id+"F0.wireOp",EDGE,"E41");var subQ4=sQuery(id+"F0.wireOp",EDGE,"E88");var subQ5=sQuery(id+"F0.wireOp",EDGE,"E85");var subQ7=sQuery(id+"F0.wireOp",EDGE,"E82");var subQ8=sQuery(id+"F0.wireOp",EDGE,"E81");var subQ10=sQuery(id+"F0.wireOp",EDGE,"E83");var subQ12=sQuery(id+"F0.wireOp",EDGE,"E67");var subQ14=sQuery(id+"F0.wireOp",EDGE,"E91");var subQ16=sQuery(id+"F0.wireOp",EDGE,"E58");var subQ17=sQuery(id+"F0.wireOp",EDGE,"E57");var subQ19=sQuery(id+"F0.wireOp",EDGE,"E105");var subQ21=sQuery(id+"F0.wireOp",EDGE,"E59");var subQ22=makeQuery(id+"F1.opExtrude","SWEPT_FACE",FACE,{"disambiguationData":[OSD([subQ21])]});var subQ23=sQuery(id+"F0.wireOp",EDGE,"E64");var subQ24=sQuery(id+"F0.wireOp",EDGE,"E61");var subQ26=sQuery(id+"F0.wireOp",EDGE,"E111");var subQ28=sQuery(id+"F0.wireOp",EDGE,"E65");var subQ36=sQuery(id+"F0.wireOp",EDGE,"E55");var subQ38=sQuery(id+"F0.wireOp",EDGE,"E53");var subQ40=sQuery(id+"F0.wireOp",EDGE,"E51");var subQ42=sQuery(id+"F0.wireOp",EDGE,"E52");var subQ43=sQuery(id+"F0.wireOp",EDGE,"E49");var subQ45=sQuery(id+"F0.wireOp",EDGE,"E47");var subQ47=sQuery(id+"F0.wireOp",EDGE,"E46");var subQ48=sQuery(id+"F0.wireOp",EDGE,"E45");var subQ50=sQuery(id+"F0.wireOp",EDGE,"E126");var subQ51=sQuery(id+"F0.wireOp",EDGE,"E36");var subQ53=sQuery(id+"F0.wireOp",EDGE,"E117");var subQ54=sQuery(id+"F0.wireOp",EDGE,"E35");var subQ56=sQuery(id+"F0.wireOp",EDGE,"E114");var subQ57=sQuery(id+"F0.wireOp",EDGE,"E34");var subQ59=sQuery(id+"F0.wireOp",EDGE,"E33");var subQ61=sQuery(id+"F0.wireOp",EDGE,"E108");var subQ62=sQuery(id+"F0.wireOp",EDGE,"E32");var subQ65=sQuery(id+"F0.wireOp",EDGE,"E31");var subQ71=sQuery(id+"F0.wireOp",EDGE,"E102");var subQ72=sQuery(id+"F0.wireOp",EDGE,"E30");var subQ76=sQuery(id+"F0.wireOp",EDGE,"E44");var subQ77=sQuery(id+"F0.wireOp",EDGE,"E29");var subQ79=sQuery(id+"F0.wireOp",EDGE,"E28");var subQ81=sQuery(id+"F0.wireOp",EDGE,"E27");var subQ83=sQuery(id+"F0.wireOp",EDGE,"E26");var subQ87=sQuery(id+"F0.wireOp",EDGE,"E25");var subQ89=sQuery(id+"F0.wireOp",EDGE,"E24");var subQ91=sQuery(id+"F0.wireOp",EDGE,"E23");var subQ94=sQuery(id+"F0.wireOp",EDGE,"E9");var subQ96=sQuery(id+"F0.wireOp",EDGE,"E7");var subQ98=sQuery(id+"F0.wireOp",EDGE,"E6");var subQ100=sQuery(id+"F0.wireOp",EDGE,"E5");var subQ102=sQuery(id+"F0.wireOp",EDGE,"E4");var subQ104=sQuery(id+"F0.wireOp",EDGE,"E10");var subQ106=sQuery(id+"F0.wireOp",EDGE,"E0");var subQ107=makeQuery(id+"F1.opExtrude","SWEPT_FACE",FACE,{"disambiguationData":[OSD([subQ106])]});var subQ108=sQuery(id+"F0.wireOp",EDGE,"E22");var subQ111=sQuery(id+"F0.wireOp",EDGE,"E3");var subQ113=sQuery(id+"F0.wireOp",EDGE,"E1");var subQ115=sQuery(id+"F0.wireOp",EDGE,"E63");var subQ117=sQuery(id+"F0.wireOp",EDGE,"E2");var subQ119=sQuery(id+"F0.wireOp",EDGE,"E11");var subQ121=sQuery(id+"F0.wireOp",EDGE,"E12");var subQ123=sQuery(id+"F0.wireOp",EDGE,"E13");var subQ125=sQuery(id+"F0.wireOp",EDGE,"E14");var subQ127=sQuery(id+"F0.wireOp",EDGE,"E15");var subQ129=sQuery(id+"F0.wireOp",EDGE,"E16");var subQ131=sQuery(id+"F0.wireOp",EDGE,"E17");var subQ134=sQuery(id+"F0.wireOp",EDGE,"E18");var subQ136=sQuery(id+"F0.wireOp",EDGE,"E19");var subQ138=sQuery(id+"F0.wireOp",EDGE,"E20");var subQ141=sQuery(id+"F0.wireOp",EDGE,"E21");var subQ144=sQuery(id+"F0.wireOp",EDGE,"E70");var subQ145=sQuery(id+"F0.wireOp",EDGE,"E69");var subQ147=sQuery(id+"F0.wireOp",EDGE,"E71");var subQ149=sQuery(id+"F0.wireOp",EDGE,"E76");var subQ150=sQuery(id+"F0.wireOp",EDGE,"E73");var subQ152=sQuery(id+"F0.wireOp",EDGE,"E75");var subQ154=sQuery(id+"F0.wireOp",EDGE,"E77");var subQ156=sQuery(id+"F0.wireOp",EDGE,"E79");var subQ158=sQuery(id+"F0.wireOp",EDGE,"E80");var subQ160=sQuery(id+"F0.wireOp",EDGE,"E87");var subQ162=sQuery(id+"F0.wireOp",EDGE,"E90");var subQ164=sQuery(id+"F0.wireOp",EDGE,"E120");var subQ165=sQuery(id+"F0.wireOp",EDGE,"E123");var subQ166=sQuery(id+"F0.wireOp",EDGE,"E129");var subQ167=sQuery(id+"F0.wireOp",EDGE,"E132");var subQ168=sQuery(id+"F0.wireOp",EDGE,"E135");var subQ169=sQuery(id+"F0.wireOp",EDGE,"E138");var subQ170=sQuery(id+"F0.wireOp",EDGE,"E141");Q1=makeQuery(id+"F11.boolean.opBoolean","SPLIT",FACE,{"disambiguationData":[TD([subQ22])],"derivedFrom":makeQuery(id+"F8.boolean.opBoolean","SPLIT",FACE,{"disambiguationData":[TD([subQ107])],"derivedFrom":makeQuery(id+"F3.boolean.opBoolean","SPLIT",FACE,{"disambiguationData":[TD([subQ107])],"derivedFrom":makeQuery(id+"F1.opExtrude","CAP_FACE",FACE,{"disambiguationData":[OSD([subQ106,subQ113,subQ117,subQ111,subQ102,subQ100,subQ98,subQ96,subQ94,subQ104,subQ119,subQ121,subQ123,subQ125,subQ127,subQ129,subQ131,subQ134,subQ136,subQ138,subQ141,subQ108,subQ91,subQ89,subQ87,subQ83,subQ81,subQ79,subQ77,subQ72,subQ65,subQ62,subQ59,subQ57,subQ54,subQ51,subQ2,subQ76,subQ48,subQ47,subQ45,subQ43,subQ40,subQ42,subQ38,sQuery(id+"F0.wireOp",EDGE,"E54"),subQ36,sQuery(id+"F0.wireOp",EDGE,"E56"),subQ17,subQ16,subQ21,subQ24,subQ115,subQ23,subQ28,sQuery(id+"F0.wireOp",EDGE,"E66"),subQ12,sQuery(id+"F0.wireOp",EDGE,"E68"),subQ145,subQ144,subQ147,subQ150,subQ152,subQ149,subQ154,sQuery(id+"F0.wireOp",EDGE,"E78"),subQ156,subQ158,subQ8,subQ7,subQ10,subQ5,subQ160,subQ4,subQ0,subQ162,subQ14,sQuery(id+"F0.wireOp",EDGE,"E92"),sQuery(id+"F0.wireOp",EDGE,"E93"),subQ71,subQ19,subQ61,subQ26,subQ56,subQ53,subQ164,subQ165,subQ50,subQ166,subQ167,subQ168,subQ169,subQ170,sQuery(id+"F0.wireOp",EDGE,"E144")])],"isStart":true})})})});}
            extrude(context, id + "F13", {"entities" : qUnion([Q0]), "operationType" : NewBodyOperationType.REMOVE, "endBound" : BoundingType.UP_TO_SURFACE, "oppositeDirection" : true, "depth" : 25 * mm, "endBoundEntityFace" : qUnion([Q1]), "offsetDistance" : 25 * mm});
        }
        {
            var Q0;
            {var subQ0=sQuery(id+"F7.wireOp",EDGE,"E188");var subQ2=sQuery(id+"F12.wireOp",EDGE,"E213");Q0=makeQuery(id+"F13.boolean.opBoolean","COPY",EDGE,{"disambiguationData":[TD([makeQuery(id+"F8.opExtrude","SWEPT_FACE",FACE,{"disambiguationData":[OSD([subQ0])]})])],"derivedFrom":makeQuery(id+"F13.opExtrude","CAP_EDGE",EDGE,{"disambiguationData":[OSD([subQ2])],"isStart":true})});}
            var Q1;
            {var subQ0=sQuery(id+"F7.wireOp",EDGE,"E190");var subQ2=sQuery(id+"F12.wireOp",EDGE,"E212");Q1=makeQuery(id+"F13.boolean.opBoolean","COPY",EDGE,{"disambiguationData":[TD([makeQuery(id+"F8.opExtrude","SWEPT_FACE",FACE,{"disambiguationData":[OSD([subQ0])]})])],"derivedFrom":makeQuery(id+"F13.opExtrude","CAP_EDGE",EDGE,{"disambiguationData":[OSD([subQ2])],"isStart":true})});}
            var Q2;
            {var subQ0=sQuery(id+"F7.wireOp",EDGE,"E189");var subQ2=sQuery(id+"F12.wireOp",EDGE,"E212");Q2=makeQuery(id+"F13.boolean.opBoolean","COPY",EDGE,{"disambiguationData":[TD([makeQuery(id+"F8.opExtrude","SWEPT_FACE",FACE,{"disambiguationData":[OSD([subQ0])]})])],"derivedFrom":makeQuery(id+"F13.opExtrude","CAP_EDGE",EDGE,{"disambiguationData":[OSD([subQ2])],"isStart":true})});}
            var Q3;
            {var subQ0=sQuery(id+"F7.wireOp",EDGE,"E189");var subQ2=sQuery(id+"F12.wireOp",EDGE,"E213");Q3=makeQuery(id+"F13.boolean.opBoolean","COPY",EDGE,{"disambiguationData":[TD([makeQuery(id+"F8.opExtrude","SWEPT_FACE",FACE,{"disambiguationData":[OSD([subQ0])]})])],"derivedFrom":makeQuery(id+"F13.opExtrude","CAP_EDGE",EDGE,{"disambiguationData":[OSD([subQ2])],"isStart":true})});}
            chamfer(context, id + "F14", {"entities" : qUnion([Q0, Q1, Q2, Q3]), "chamferType" : ChamferType.OFFSET_ANGLE, "width" : 9 * mm, "oppositeDirection" : false, "angle" : 5 * degree, "tangentPropagation" : true});
        }
    });
